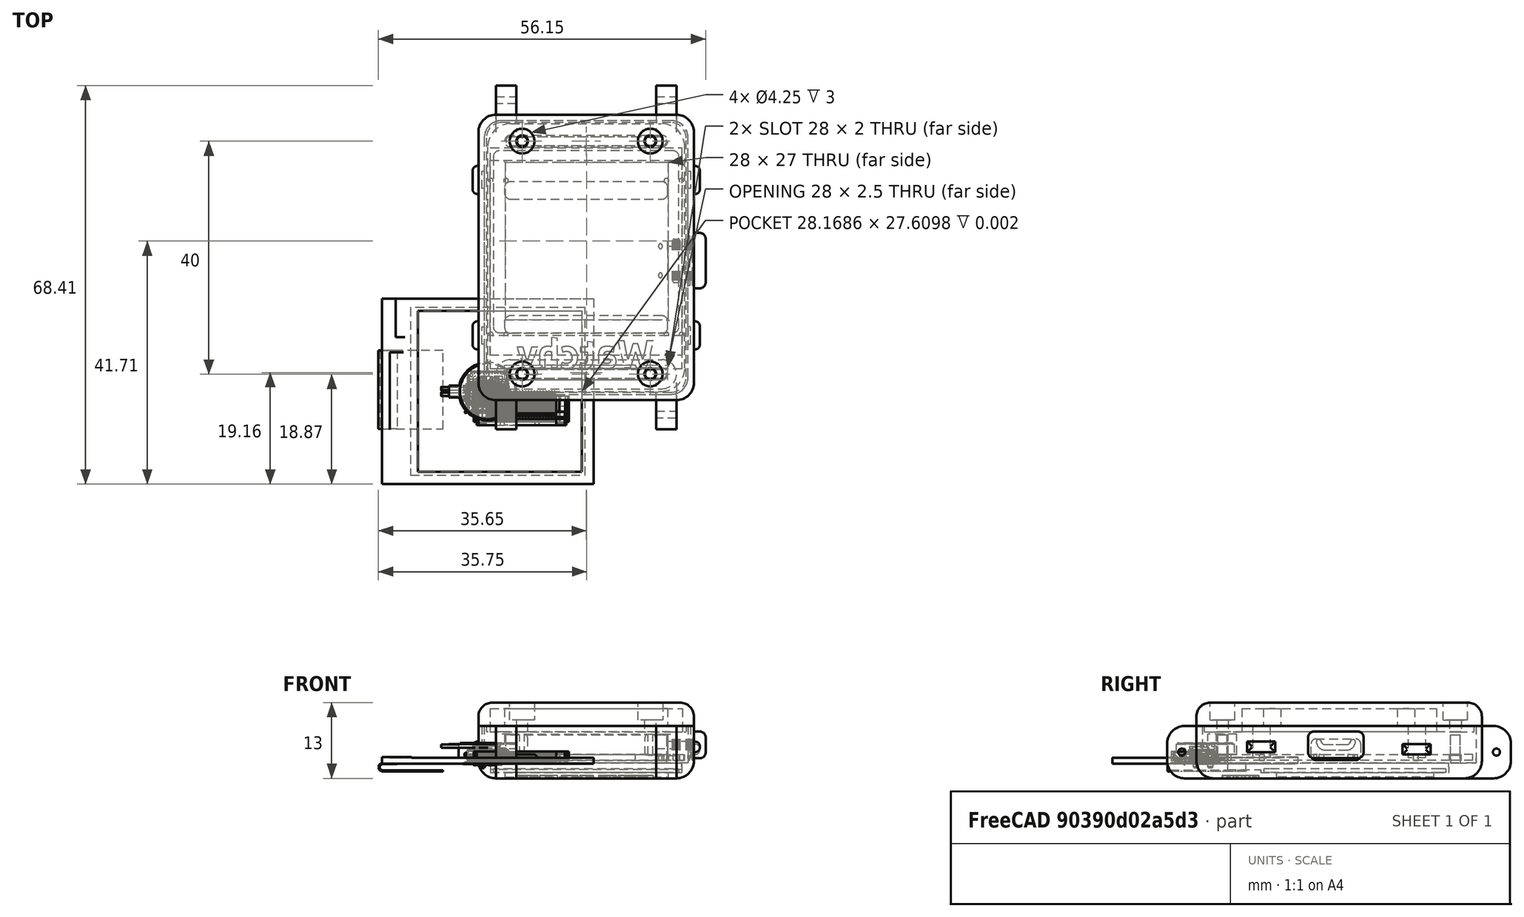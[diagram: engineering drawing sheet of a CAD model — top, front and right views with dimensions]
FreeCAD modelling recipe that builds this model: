
FCSTD DOCUMENT  (FreeCAD 0.20R29177 +426 (Git))
Label: JJ-WATCHY
License: All rights reserved
LicenseURL: http://en.wikipedia.org/wiki/All_rights_reserved
objects: Part::Feature×58, App::Part×56, Sketcher::SketchObject×26, PartDesign::Pad×21, PartDesign::Pocket×14, PartDesign::Fillet×10, PartDesign::ShapeBinder×7, PartDesign::Body×6, PartDesign::Plane×3, Part::Part2DObjectPython×1, Part::Extrusion×1, PartDesign::FeatureBase×1, Mesh::Feature×1, Part::Fuse×1, Part::Cut×1
note: 195 computed .brp shape members not serialized (recipe doc carries the construction recipe); baked Part::Feature solids carry a one-line shape summary decoded from their .brp

FEATURE [Part::Feature] Part__Feature  label="SOLID (15)"
  shape: bbox 7.981 x 5.422 x 2.941 mm, 498 faces (baked)
FEATURE [App::Part] USB_Micro_B_Molex_47346_0001  label="USB_Micro-B_Molex_47346-0001"
  Group = -> [Part__Feature]
  Origin = -> Origin
  Placement = pos=(31.38,22.43,1.65) rot=(0,0,1;1.5708rad)
FEATURE [Part::Feature] Part__Feature001  label="SOLID"
  shape: bbox 1.6 x 0.8 x 0.8 mm, 28 faces (baked)
FEATURE [App::Part] C_0603_1608Metric
  Group = -> [Part__Feature001]
  Origin = -> Origin001
  Placement = pos=(5.16,37.71,1.65) rot=(0,0,1;0rad)
FEATURE [Part::Feature] Part__Feature002  label="SOLID (16)"
  shape: bbox 6.669 x 4.906 x 2.452 mm, 452 faces (baked)
FEATURE [App::Part] Button
  Group = -> [Part__Feature002]
  Origin = -> Origin002
  Placement = pos=(2.38,35.43,1.65) rot=(0,0,-1;1.5708rad)
FEATURE [Part::Feature] Part__Feature003  label="SOLID (16)001"
  shape: bbox 6.669 x 4.906 x 2.452 mm, 452 faces (baked)
FEATURE [App::Part] Button001
  Group = -> [Part__Feature003]
  Origin = -> Origin003
  Placement = pos=(2.38,8.73,1.65) rot=(0,0,-1;1.5708rad)
FEATURE [Part::Feature] Part__Feature004  label="SOLID (16)002"
  shape: bbox 6.669 x 4.906 x 2.452 mm, 452 faces (baked)
FEATURE [App::Part] Button002
  Group = -> [Part__Feature004]
  Origin = -> Origin004
  Placement = pos=(31.42,37.23,1.65) rot=(0,0,1;1.5708rad)
FEATURE [Part::Feature] Part__Feature005  label="SOLID (16)003"
  shape: bbox 6.669 x 4.906 x 2.452 mm, 452 faces (baked)
FEATURE [App::Part] Button003
  Group = -> [Part__Feature005]
  Origin = -> Origin005
  Placement = pos=(31.42,10.53,1.65) rot=(0,0,1;1.5708rad)
FEATURE [Part::Feature] Part__Feature006  label="SOLID (1)"
  shape: bbox 2 x 2 x 1.025 mm, 68 faces (baked)
FEATURE [App::Part] LGA_12_2x2mm_P0_5mm  label="LGA-12_2x2mm_P0.5mm"
  Group = -> [Part__Feature006]
  Origin = -> Origin006
  Placement = pos=(10.76,34.89,1.65) rot=(0,0,1;3.14159rad)
FEATURE [Part::Feature] Part__Feature007  label="COMPOUND (3)"
  shape: bbox 16.3 x 5.85 x 2.11 mm, 1280 faces, 17 solids (baked)
FEATURE [App::Part] FPC_24  label="FPC-24"
  Group = -> [Part__Feature007]
  Origin = -> Origin007
  Placement = pos=(11.025,19.09,1.65) rot=(0,0,1;0rad)
FEATURE [Part::Feature] Part__Feature008  label="SOLID (4)"
  shape: bbox 7.65 x 5.2 x 3.4 mm, 136 faces (baked)
FEATURE [App::Part] Molex_PicoBlade_53261_0271_1x02_1MP_P1_25mm_Horizontal  label="Molex_PicoBlade_53261-0271_1x02-1MP_P1.25mm_Horizontal"
  Group = -> [Part__Feature008]
  Origin = -> Origin008
  Placement = pos=(28.63,31.39,1.65) rot=(0,0,-1;1.5708rad)
FEATURE [Part::Feature] Part__Feature009  label="SOLID (2)"
  shape: bbox 1 x 0.5 x 0.35 mm, 26 faces (baked)
FEATURE [App::Part] R_0402_1005Metric
  Group = -> [Part__Feature009]
  Origin = -> Origin009
  Placement = pos=(31.7,28.28,1.65) rot=(0,0,1;1.5708rad)
FEATURE [Part::Feature] Part__Feature010  label="SOLID (5)"
  shape: bbox 4 x 4 x 1.1 mm, 158 faces (baked)
FEATURE [App::Part] QFN_24_1EP_4x4mm_P0_5mm_EP2_7x2_7mm  label="QFN-24-1EP_4x4mm_P0.5mm_EP2.7x2.7mm"
  Group = -> [Part__Feature010]
  Origin = -> Origin010
  Placement = pos=(25.76,24.38,1.65) rot=(0,0,1;0rad)
FEATURE [Part::Feature] Part__Feature011  label="SOLID (2)001"
  shape: bbox 1 x 0.5 x 0.35 mm, 26 faces (baked)
FEATURE [App::Part] R_0402_1005Metric001
  Group = -> [Part__Feature011]
  Origin = -> Origin011
  Placement = pos=(29.05,13.07,1.65) rot=(0,0,1;0rad)
FEATURE [Part::Feature] Part__Feature012  label="SOLID001"
  shape: bbox 1.6 x 0.8 x 0.8 mm, 28 faces (baked)
FEATURE [App::Part] C_0603_1608Metric001
  Group = -> [Part__Feature012]
  Origin = -> Origin012
  Placement = pos=(21.71,23.42,1.65) rot=(0,0,1;0rad)
FEATURE [Part::Feature] Part__Feature013  label="COMPOUND"
  shape: bbox 37.16 x 32.08 x 2.7 mm, 57 faces, 2 solids (baked)
FEATURE [App::Part] Display
  Group = -> [Part__Feature013]
  Origin = -> Origin013
  Placement = pos=(16.89,23.15,0.55) rot=(0.707107,0.707107,0;3.14159rad)
FEATURE [Part::Feature] Part__Feature014  label="SOLID002"
  shape: bbox 1.6 x 0.8 x 0.8 mm, 28 faces (baked)
FEATURE [App::Part] C_0603_1608Metric002
  Group = -> [Part__Feature014]
  Origin = -> Origin014
  Placement = pos=(15.42,35.06,1.65) rot=(0,0,1;1.5708rad)
FEATURE [Part::Feature] Part__Feature015  label="SOLID003"
  shape: bbox 1.6 x 0.8 x 0.8 mm, 28 faces (baked)
FEATURE [App::Part] C_0603_1608Metric003
  Group = -> [Part__Feature015]
  Origin = -> Origin015
  Placement = pos=(19.01,21.47,1.65) rot=(0,0,1;1.5708rad)
FEATURE [Part::Feature] Part__Feature016  label="SOLID (3)"
  shape: bbox 2 x 1.25 x 1.25 mm, 28 faces (baked)
FEATURE [App::Part] C_0805_2012Metric
  Group = -> [Part__Feature016]
  Origin = -> Origin016
  Placement = pos=(5.63,12.59,1.65) rot=(0,0,1;0rad)
FEATURE [Part::Feature] Part__Feature017  label="SOLID (3)001"
  shape: bbox 2 x 1.25 x 1.25 mm, 28 faces (baked)
FEATURE [App::Part] C_0805_2012Metric001
  Group = -> [Part__Feature017]
  Origin = -> Origin017
  Placement = pos=(6.63,6.34,1.65) rot=(0,0,1;0rad)
FEATURE [Part::Feature] Part__Feature018  label="SOLID004"
  shape: bbox 1.6 x 0.8 x 0.8 mm, 28 faces (baked)
FEATURE [App::Part] C_0603_1608Metric004
  Group = -> [Part__Feature018]
  Origin = -> Origin018
  Placement = pos=(13.81,21.47,1.65) rot=(0,0,1;1.5708rad)
FEATURE [Part::Feature] Part__Feature019  label="SOLID005"
  shape: bbox 1.6 x 0.8 x 0.8 mm, 28 faces (baked)
FEATURE [App::Part] C_0603_1608Metric005
  Group = -> [Part__Feature019]
  Origin = -> Origin019
  Placement = pos=(16.41,21.47,1.65) rot=(0,0,1;1.5708rad)
FEATURE [Part::Feature] Part__Feature020  label="SOLID006"
  shape: bbox 1.6 x 0.8 x 0.8 mm, 28 faces (baked)
FEATURE [App::Part] C_0603_1608Metric006
  Group = -> [Part__Feature020]
  Origin = -> Origin020
  Placement = pos=(17.71,21.47,1.65) rot=(0,0,1;1.5708rad)
FEATURE [Part::Feature] Part__Feature021  label="SOLID007"
  shape: bbox 1.6 x 0.8 x 0.8 mm, 28 faces (baked)
FEATURE [App::Part] C_0603_1608Metric007
  Group = -> [Part__Feature021]
  Origin = -> Origin021
  Placement = pos=(15.11,21.47,1.65) rot=(0,0,1;1.5708rad)
FEATURE [Part::Feature] Part__Feature022  label="SOLID008"
  shape: bbox 1.6 x 0.8 x 0.8 mm, 28 faces (baked)
FEATURE [App::Part] C_0603_1608Metric008
  Group = -> [Part__Feature022]
  Origin = -> Origin022
  Placement = pos=(12.46,21.47,1.65) rot=(0,0,1;1.5708rad)
FEATURE [Part::Feature] Part__Feature023  label="SOLID009"
  shape: bbox 1.6 x 0.8 x 0.8 mm, 28 faces (baked)
FEATURE [App::Part] C_0603_1608Metric009
  Group = -> [Part__Feature023]
  Origin = -> Origin023
  Placement = pos=(11.16,21.47,1.65) rot=(0,0,1;1.5708rad)
FEATURE [Part::Feature] Part__Feature024  label="SOLID (3)002"
  shape: bbox 2 x 1.25 x 1.25 mm, 28 faces (baked)
FEATURE [App::Part] C_0805_2012Metric002
  Group = -> [Part__Feature024]
  Origin = -> Origin024
  Placement = pos=(17.82,35.53,1.65) rot=(0,0,1;3.14159rad)
FEATURE [Part::Feature] Part__Feature025  label="SOLID (6)"
  shape: bbox 3.8 x 1.6 x 1.25 mm, 67 faces (baked)
FEATURE [App::Part] D_SOD_123  label="D_SOD-123"
  Group = -> [Part__Feature025]
  Origin = -> Origin025
  Placement = pos=(1.25,15.82,1.65) rot=(0,0,1;1.5708rad)
FEATURE [Part::Feature] Part__Feature026  label="SOLID (6)001"
  shape: bbox 3.8 x 1.6 x 1.25 mm, 67 faces (baked)
FEATURE [App::Part] D_SOD_123001  label="D_SOD-124"
  Group = -> [Part__Feature026]
  Origin = -> Origin026
  Placement = pos=(3.55,15.82,1.65) rot=(0,0,-1;1.5708rad)
FEATURE [Part::Feature] Part__Feature027  label="SOLID (6)002"
  shape: bbox 3.8 x 1.6 x 1.25 mm, 67 faces (baked)
FEATURE [App::Part] D_SOD_123002  label="D_SOD-125"
  Group = -> [Part__Feature027]
  Origin = -> Origin027
  Placement = pos=(5.85,15.82,1.65) rot=(0,0,-1;1.5708rad)
FEATURE [Part::Feature] Part__Feature028  label="SOLID (6)003"
  shape: bbox 3.8 x 1.6 x 1.25 mm, 67 faces (baked)
FEATURE [App::Part] D_SOD_123003  label="D_SOD-126"
  Group = -> [Part__Feature028]
  Origin = -> Origin028
  Placement = pos=(27.27,19.28,1.65) rot=(0,0,1;1.5708rad)
FEATURE [Part::Feature] Part__Feature029  label="SOLID (7)"
  shape: bbox 1.6 x 0.8 x 1.1 mm, 50 faces (baked)
FEATURE [App::Part] LED_0603_1608Metric
  Group = -> [Part__Feature029]
  Origin = -> Origin029
  Placement = pos=(33.04,30.53,1.65) rot=(0,0,1;1.5708rad)
FEATURE [Part::Feature] Part__Feature030  label="SOLID (8)"
  shape: bbox 3.5 x 1.6 x 1.1 mm, 27 faces (baked)
FEATURE [App::Part] D_SOD_123F  label="D_SOD-123F"
  Group = -> [Part__Feature030]
  Origin = -> Origin030
  Placement = pos=(4.91,34.705,1.65) rot=(0,0,-1;1.5708rad)
FEATURE [Part::Feature] Part__Feature031  label="SOLID (9)"
  shape: bbox 3.2 x 2.5 x 2.5 mm, 28 faces (baked)
FEATURE [App::Part] L_1210_3225Metric
  Group = -> [Part__Feature031]
  Origin = -> Origin031
  Placement = pos=(6.13,9.47,1.65) rot=(0,0,-1;1.5708rad)
FEATURE [Part::Feature] Part__Feature032  label="SOLID (10)"
  shape: bbox 2.5 x 3 x 1.2 mm, 76 faces (baked)
FEATURE [App::Part] SOT_23  label="SOT-23"
  Group = -> [Part__Feature032]
  Origin = -> Origin032
  Placement = pos=(28.1,9.03,1.65) rot=(0,0,-1;1.5708rad)
FEATURE [Part::Feature] Part__Feature033  label="SOLID (10)001"
  shape: bbox 2.5 x 3 x 1.2 mm, 76 faces (baked)
FEATURE [App::Part] SOT_23001  label="SOT-024"
  Group = -> [Part__Feature033]
  Origin = -> Origin033
  Placement = pos=(28.45,15.23,1.65) rot=(0,0,-1;1.5708rad)
FEATURE [Part::Feature] Part__Feature034  label="SOLID (10)002"
  shape: bbox 2.5 x 3 x 1.2 mm, 76 faces (baked)
FEATURE [App::Part] SOT_23002  label="SOT-025"
  Group = -> [Part__Feature034]
  Origin = -> Origin034
  Placement = pos=(7.81,35.31,1.65) rot=(0,0,1;3.14159rad)
FEATURE [Part::Feature] Part__Feature035  label="SOLID (2)002"
  shape: bbox 1 x 0.5 x 0.35 mm, 26 faces (baked)
FEATURE [App::Part] R_0402_1005Metric002
  Group = -> [Part__Feature035]
  Origin = -> Origin035
  Placement = pos=(16.97,34.19,1.65) rot=(0,0,1;3.14159rad)
FEATURE [Part::Feature] Part__Feature036  label="SOLID (2)003"
  shape: bbox 1 x 0.5 x 0.35 mm, 26 faces (baked)
FEATURE [App::Part] R_0402_1005Metric003
  Group = -> [Part__Feature036]
  Origin = -> Origin036
  Placement = pos=(22.55,26.67,1.65) rot=(0,0,1;1.5708rad)
FEATURE [Part::Feature] Part__Feature037  label="SOLID (2)004"
  shape: bbox 1 x 0.5 x 0.35 mm, 26 faces (baked)
FEATURE [App::Part] R_0402_1005Metric004
  Group = -> [Part__Feature037]
  Origin = -> Origin037
  Placement = pos=(23.91,27.48,1.65) rot=(0,0,1;3.14159rad)
FEATURE [Part::Feature] Part__Feature038  label="SOLID (2)005"
  shape: bbox 1 x 0.5 x 0.35 mm, 26 faces (baked)
FEATURE [App::Part] R_0402_1005Metric005
  Group = -> [Part__Feature038]
  Origin = -> Origin038
  Placement = pos=(27.15,13.07,1.65) rot=(0,0,1;3.14159rad)
FEATURE [Part::Feature] Part__Feature039  label="SOLID (2)006"
  shape: bbox 1 x 0.5 x 0.35 mm, 26 faces (baked)
FEATURE [App::Part] R_0402_1005Metric006
  Group = -> [Part__Feature039]
  Origin = -> Origin039
  Placement = pos=(28.66,36.44,1.65) rot=(0,0,1;0rad)
FEATURE [Part::Feature] Part__Feature040  label="SOLID (2)007"
  shape: bbox 1 x 0.5 x 0.35 mm, 26 faces (baked)
FEATURE [App::Part] R_0402_1005Metric007
  Group = -> [Part__Feature040]
  Origin = -> Origin040
  Placement = pos=(6.69,32.68,1.65) rot=(0,0,-1;1.5708rad)
FEATURE [Part::Feature] Part__Feature041  label="SOLID (2)008"
  shape: bbox 1 x 0.5 x 0.35 mm, 26 faces (baked)
FEATURE [App::Part] R_0402_1005Metric008
  Group = -> [Part__Feature041]
  Origin = -> Origin041
  Placement = pos=(29.05,11.28,1.65) rot=(0,0,1;3.14159rad)
FEATURE [Part::Feature] Part__Feature042  label="SOLID (2)009"
  shape: bbox 1 x 0.5 x 0.35 mm, 26 faces (baked)
FEATURE [App::Part] R_0402_1005Metric009
  Group = -> [Part__Feature042]
  Origin = -> Origin042
  Placement = pos=(27.15,11.28,1.65) rot=(0,0,1;3.14159rad)
FEATURE [Part::Feature] Part__Feature043  label="SOLID (2)010"
  shape: bbox 1 x 0.5 x 0.35 mm, 26 faces (baked)
FEATURE [App::Part] R_0402_1005Metric010
  Group = -> [Part__Feature043]
  Origin = -> Origin043
  Placement = pos=(4.35,6.34,1.65) rot=(0,0,1;1.5708rad)
FEATURE [Part::Feature] Part__Feature044  label="SOLID (2)011"
  shape: bbox 1 x 0.5 x 0.35 mm, 26 faces (baked)
FEATURE [App::Part] R_0402_1005Metric011
  Group = -> [Part__Feature044]
  Origin = -> Origin044
  Placement = pos=(30.8,28.28,1.65) rot=(0,0,1;1.5708rad)
FEATURE [Part::Feature] Part__Feature045  label="SOLID (2)012"
  shape: bbox 1 x 0.5 x 0.35 mm, 26 faces (baked)
FEATURE [App::Part] R_0402_1005Metric012
  Group = -> [Part__Feature045]
  Origin = -> Origin045
  Placement = pos=(29.32,17.4,1.65) rot=(0,0,1;3.14159rad)
FEATURE [Part::Feature] Part__Feature046  label="SOLID (2)013"
  shape: bbox 1 x 0.5 x 0.35 mm, 26 faces (baked)
FEATURE [App::Part] R_0402_1005Metric013
  Group = -> [Part__Feature046]
  Origin = -> Origin046
  Placement = pos=(33.24,28.28,1.65) rot=(0,0,-1;1.5708rad)
FEATURE [Part::Feature] Part__Feature047  label="SOLID (2)014"
  shape: bbox 1 x 0.5 x 0.35 mm, 26 faces (baked)
FEATURE [App::Part] R_0402_1005Metric014
  Group = -> [Part__Feature047]
  Origin = -> Origin047
  Placement = pos=(7.75,32.68,1.65) rot=(0,0,-1;1.5708rad)
FEATURE [Part::Feature] Part__Feature048  label="SOLID (13)"
  shape: bbox 7 x 7 x 0.77 mm, 302 faces (baked)
FEATURE [App::Part] QFN_48_1EP_7x7mm_P0_5mm_EP5_15x5_15mm  label="QFN-48-1EP_7x7mm_P0.5mm_EP5.15x5.15mm"
  Group = -> [Part__Feature048]
  Origin = -> Origin048
  Placement = pos=(17.7737,29.6588,1.65) rot=(0,0,-1;1.5708rad)
FEATURE [Part::Feature] Part__Feature049  label="SOLID (11)"
  shape: bbox 2.8 x 2.9 x 1.55 mm, 109 faces (baked)
FEATURE [App::Part] SOT_23_5  label="SOT-23-5"
  Group = -> [Part__Feature049]
  Origin = -> Origin049
  Placement = pos=(24.66,19.88,1.65) rot=(0,0,-1;1.5708rad)
FEATURE [Part::Feature] Part__Feature050  label="SOLID (11)001"
  shape: bbox 2.8 x 2.9 x 1.55 mm, 109 faces (baked)
FEATURE [App::Part] SOT_23_5001  label="SOT-23-006"
  Group = -> [Part__Feature050]
  Origin = -> Origin050
  Placement = pos=(32,15.93,1.65) rot=(0,0,-1;1.5708rad)
FEATURE [Part::Feature] Part__Feature051  label="SOLID (12)"
  shape: bbox 2 x 2 x 1.05 mm, 118 faces (baked)
FEATURE [App::Part] SOT_363_SC_70_6  label="SOT-363_SC-70-6"
  Group = -> [Part__Feature051]
  Origin = -> Origin051
  Placement = pos=(21.31,21.47,1.65) rot=(0,0,1;3.14159rad)
FEATURE [Part::Feature] Part__Feature052  label="SOLID (14)"
  shape: bbox 6 x 4.9 x 1.75 mm, 156 faces (baked)
FEATURE [App::Part] SOIC_8_3_9x4_9mm_P1_27mm  label="SOIC-8_3.9x4.9mm_P1.27mm"
  Group = -> [Part__Feature052]
  Origin = -> Origin052
  Placement = pos=(11.07,29.81,1.65) rot=(0,0,1;1.5708rad)
FEATURE [Part::Feature] Part__Feature053  label="SOLID (2)015"
  shape: bbox 1 x 0.5 x 0.35 mm, 26 faces (baked)
FEATURE [App::Part] R_0402_1005Metric015
  Group = -> [Part__Feature053]
  Origin = -> Origin053
  Placement = pos=(7.75,30.52,1.65) rot=(0,0,-1;1.5708rad)
FEATURE [Part::Feature] Part__Feature054  label="COMPOUND (1)"
  shape: bbox 13 x 10 x 2.5 mm, 15 faces, 3 solids (baked)
FEATURE [App::Part] PagerMotor
  Group = -> [Part__Feature054]
  Origin = -> Origin054
  Placement = pos=(5.45,22.955,5.15) rot=(0.819152,-0.573576,0;3.14159rad)
FEATURE [Part::Feature] Part__Feature055  label="COMPOUND (2)"
  shape: bbox 33.8 x 45.96 x 1 mm, 46 faces (baked)
FEATURE [App::Part] Watchy_Fixed_Dimensions_v1  label="Watchy Fixed Dimensions v1"
  Group = -> [USB_Micro_B_Molex_47346_0001,C_0603_1608Metric,Button,Button001,Button002,Button003,LGA_12_2x2mm_P0_5mm,FPC_24,Molex_PicoBlade_53261_0271_1x02_1MP_P1_25mm_Horizontal,R_0402_1005Metric,QFN_24_1EP_4x4mm_P0_5mm_EP2_7x2_7mm,R_0402_1005Metric001,C_0603_1608Metric001,Display,C_0603_1608Metric002,C_0603_1608Metric003,C_0805_2012Metric,C_0805_2012Metric001,C_0603_1608Metric004,C_0603_1608Metric005,+36 more]
  Origin = -> Origin055
  Placement = pos=(0,0,-0.43) rot=(0,0,1;0rad)
FEATURE [Sketcher::SketchObject] Sketch
  FullyConstrained = true
  MapMode = 5
  Placement = pos=(0,0,0) rot=(0,1,0;3.14159rad)
  Support = -> [XY_Plane056]
  sketch-geometry (4):
    g0: LineSegment StartX=-32.81 StartY=41.31 StartZ=0 EndX=-0.98 EndY=41.31 EndZ=0
    g1: LineSegment StartX=-0.98 StartY=41.31 StartZ=0 EndX=-0.98 EndY=10.07 EndZ=0
    g2: LineSegment StartX=-0.98 StartY=10.07 StartZ=0 EndX=-32.81 EndY=10.07 EndZ=0
    g3: LineSegment StartX=-32.81 StartY=10.07 StartZ=0 EndX=-32.81 EndY=41.31 EndZ=0
  constraints (12):
    c: Coincident(g0,g1)
    c: Coincident(g1,g2)
    c: Coincident(g2,g3)
    c: Coincident(g3,g0)
    c: Horizontal(g0)
    c: Horizontal(g2)
    c: Vertical(g1)
    c: Vertical(g3)
    c: DistanceX(g0,g0) = 31.83
    c: DistanceY(g1,g1) = 31.24
    c: DistanceY(g-1,g1) = 10.07
    c: DistanceX(g1,g-1) = 0.98
FEATURE [PartDesign::Pad] Pad
  Direction = (0,0,-1)
  Length = 1.5
  Length2 = 10
  Profile = -> Sketch
  ReferenceAxis = -> Sketch [N_Axis]
  Type = 0
FEATURE [PartDesign::Fillet] Fillet
  Base = -> Pad [Edge1,Edge2,Edge5,Edge8]
  BaseFeature = -> Pad
  Radius = 1
  SupportTransform = false
  UseAllEdges = false
FEATURE [PartDesign::Pocket] Pocket
  BaseFeature = -> Fillet
  Direction = (0,0,-1)
  Length = 0.9
  Length2 = 5
  Profile = -> Fillet [Face2]
  Type = 0
FEATURE [PartDesign::ShapeBinder] ReferencePocket
  Placement = pos=(0,0,-1.5) rot=(0,0,1;0rad)
  Support = -> [Pocket]
  TraceSupport = false
FEATURE [PartDesign::Plane] DatumPlane
  Length = 73.6348
  MapMode = 5
  Placement = pos=(0,0,-1.5) rot=(1,0,0;3.14159rad)
  ResizeMode = 0
  Support = -> [ReferencePocket]
  Width = 85.7348
FEATURE [Sketcher::SketchObject] Sketch001
  ExternalGeometry = -> [ReferencePocket]
  FullyConstrained = true
  MapMode = 5
  Placement = pos=(0,0,-1.5) rot=(1,0,0;3.14159rad)
  Support = -> [DatumPlane]
  sketch-geometry (5):
    g0: LineSegment StartX=-1.6 StartY=1.5 StartZ=0 EndX=35.4 EndY=1.5 EndZ=0
    g1: LineSegment StartX=35.4 StartY=1.5 StartZ=0 EndX=35.4 EndY=-47.5 EndZ=0
    g2: LineSegment StartX=35.4 StartY=-47.5 StartZ=0 EndX=-1.6 EndY=-47.5 EndZ=0
    g3: LineSegment StartX=-1.6 StartY=-47.5 StartZ=0 EndX=-1.6 EndY=1.5 EndZ=0
    g4: GeomPoint X=16.9 Y=-23 Z=0
  constraints (13):
    c: Coincident(g0,g1)
    c: Coincident(g1,g2)
    c: Coincident(g2,g3)
    c: Coincident(g3,g0)
    c: Horizontal(g0)
    c: Horizontal(g2)
    c: Vertical(g1)
    c: Vertical(g3)
    c: DistanceX(g0,g0) = 37
    c: DistanceY(g1,g1) = 49
    c: DistanceX(g-1,g4) = 16.9
    c: DistanceY(g4,g-1) = 23
    c: Symmetric(g2,g0,g4)
FEATURE [PartDesign::Pad] Pad001
  Direction = (0,0,-1)
  Length = 1
  Length2 = 8
  Placement = pos=(0,0,-1.5) rot=(1,0,0;3.14159rad)
  Profile = -> Sketch001
  ReferenceAxis = -> Sketch001 [N_Axis]
  Type = 4
FEATURE [Sketcher::SketchObject] Sketch002
  FullyConstrained = true
  MapMode = 5
  Placement = pos=(0,0,-2.5) rot=(1,0,0;3.14159rad)
  Support = -> [Pad001]
  sketch-geometry (5):
    g0: LineSegment StartX=3 StartY=-12.3 StartZ=0 EndX=31 EndY=-12.3 EndZ=0
    g1: LineSegment StartX=31 StartY=-12.3 StartZ=0 EndX=31 EndY=-39.3 EndZ=0
    g2: LineSegment StartX=31 StartY=-39.3 StartZ=0 EndX=3 EndY=-39.3 EndZ=0
    g3: LineSegment StartX=3 StartY=-39.3 StartZ=0 EndX=3 EndY=-12.3 EndZ=0
    g4: GeomPoint X=17 Y=-25.8 Z=0
  constraints (13):
    c: Coincident(g0,g1)
    c: Coincident(g1,g2)
    c: Coincident(g2,g3)
    c: Coincident(g3,g0)
    c: Horizontal(g0)
    c: Horizontal(g2)
    c: Vertical(g1)
    c: Vertical(g3)
    c: DistanceX(g0,g0) = 28
    c: DistanceY(g1,g1) = 27
    c: DistanceX(g-1,g4) = 17
    c: DistanceY(g4,g-1) = 25.8
    c: Symmetric(g2,g0,g4)
FEATURE [PartDesign::Pocket] Pocket001
  BaseFeature = -> Pad001
  Direction = (0,-1e-16,1)
  Length = 1
  Length2 = 5
  Placement = pos=(0,0,-1.5) rot=(1,0,0;3.14159rad)
  Profile = -> Sketch002
  ReferenceAxis = -> Sketch002 [N_Axis]
  Type = 0
FEATURE [Sketcher::SketchObject] Sketch003
  ExternalGeometry = -> [Pocket001]
  FullyConstrained = true
  MapMode = 5
  Placement = pos=(0,0,6.5) rot=(0,0,1;0rad)
  Support = -> [Pocket001]
  sketch-geometry (5):
    g0: LineSegment StartX=-0.6 StartY=46.5 StartZ=0 EndX=-0.6 EndY=-0.5 EndZ=0
    g1: LineSegment StartX=-0.6 StartY=-0.5 StartZ=0 EndX=34.4 EndY=-0.5 EndZ=0
    g2: LineSegment StartX=34.4 StartY=-0.5 StartZ=0 EndX=34.4 EndY=46.5 EndZ=0
    g3: LineSegment StartX=34.4 StartY=46.5 StartZ=0 EndX=-0.6 EndY=46.5 EndZ=0
    g4: Circle CenterX=16.9 CenterY=23 CenterZ=0 NormalX=0 NormalY=0 NormalZ=1 AngleXU=0 Radius=29.3002
  constraints (14):
    c: Coincident(g0,g1)
    c: Coincident(g1,g2)
    c: Coincident(g2,g3)
    c: Coincident(g3,g0)
    c: PointOnObject(g0,g4)
    c: PointOnObject(g1,g4)
    c: PointOnObject(g2,g4)
    c: PointOnObject(g3,g4)
    c: Horizontal(g3)
    c: Horizontal(g1)
    c: Vertical(g2)
    c: DistanceX(g3,g3) = 35
    c: DistanceY(g2,g2) = 47
    c: Symmetric(g-3,g-4,g4)
FEATURE [PartDesign::Pocket] Pocket002
  BaseFeature = -> Pocket001
  Direction = (0,2e-16,-1)
  Length = 7
  Length2 = 5
  Placement = pos=(0,0,-1.5) rot=(1,0,0;3.14159rad)
  Profile = -> Sketch003
  ReferenceAxis = -> Sketch003 [N_Axis]
  Type = 0
FEATURE [Sketcher::SketchObject] Sketch004
  ExternalGeometry = -> [ReferencePocket]
  FullyConstrained = true
  MapMode = 5
  Placement = pos=(0,-2e-16,-0.5) rot=(0,0,1;0rad)
  Support = -> [Pocket002]
  sketch-geometry (4):
    g0: LineSegment StartX=0.48 StartY=41.81 StartZ=0 EndX=33.31 EndY=41.81 EndZ=0
    g1: LineSegment StartX=33.31 StartY=41.81 StartZ=0 EndX=33.31 EndY=9.57 EndZ=0
    g2: LineSegment StartX=33.31 StartY=9.57 StartZ=0 EndX=0.48 EndY=9.57 EndZ=0
    g3: LineSegment StartX=0.48 StartY=9.57 StartZ=0 EndX=0.48 EndY=41.81 EndZ=0
  constraints (12):
    c: Coincident(g0,g1)
    c: Coincident(g1,g2)
    c: Coincident(g2,g3)
    c: Coincident(g3,g0)
    c: Horizontal(g0)
    c: Horizontal(g2)
    c: Vertical(g1)
    c: Vertical(g3)
    c: DistanceX(g0,g-4) = 0.5
    c: DistanceX(g-6,g0) = 0.5
    c: DistanceY(g-3,g0) = 0.5
    c: DistanceY(g1,g-5) = 0.5
FEATURE [PartDesign::Pocket] Pocket003
  BaseFeature = -> Pocket002
  Direction = (0,4e-16,-1)
  Length = 1
  Length2 = 5
  Placement = pos=(0,0,-1.5) rot=(1,0,0;3.14159rad)
  Profile = -> Sketch004
  ReferenceAxis = -> Sketch004 [N_Axis]
  Type = 0
FEATURE [Sketcher::SketchObject] Sketch005
  FullyConstrained = true
  MapMode = 5
  Placement = pos=(34.4,0,-1.5) rot=(0.57735,0.57735,-0.57735;4.18879rad)
  Support = -> [Pocket003]
  sketch-geometry (4):
    g0: LineSegment StartX=18.2 StartY=-2.15 StartZ=0 EndX=26.7 EndY=-2.15 EndZ=0
    g1: LineSegment StartX=26.7 StartY=-2.15 StartZ=0 EndX=26.7 EndY=-5.75 EndZ=0
    g2: LineSegment StartX=26.7 StartY=-5.75 StartZ=0 EndX=18.2 EndY=-5.75 EndZ=0
    g3: LineSegment StartX=18.2 StartY=-5.75 StartZ=0 EndX=18.2 EndY=-2.15 EndZ=0
  constraints (12):
    c: Coincident(g0,g1)
    c: Coincident(g1,g2)
    c: Coincident(g2,g3)
    c: Coincident(g3,g0)
    c: Horizontal(g0)
    c: Horizontal(g2)
    c: Vertical(g1)
    c: Vertical(g3)
    c: DistanceX(g2,g2) = 8.5
    c: DistanceY(g1,g1) = 3.6
    c: DistanceX(g-1,g0) = 18.2
    c: DistanceY(g0,g-1) = 2.15
FEATURE [PartDesign::Pocket] Pocket004
  BaseFeature = -> Pocket003
  Direction = (1,0,0)
  Length = 5
  Length2 = 5
  Placement = pos=(0,0,-1.5) rot=(1,0,0;3.14159rad)
  Profile = -> Sketch005
  ReferenceAxis = -> Sketch005 [N_Axis]
  Type = 0
FEATURE [Sketcher::SketchObject] Sketch006
  ExternalGeometry = -> [Pocket004]
  FullyConstrained = true
  MapMode = 5
  Placement = pos=(0,0,6.5) rot=(0,0,1;0rad)
  Support = -> [Pocket004]
  sketch-geometry (20):
    g0: LineSegment StartX=-1 StartY=37.83 StartZ=0 EndX=-0.6 EndY=37.83 EndZ=0
    g1: LineSegment StartX=-0.6 StartY=37.83 StartZ=0 EndX=-0.6 EndY=34.83 EndZ=0
    g2: LineSegment StartX=-0.6 StartY=34.83 StartZ=0 EndX=-1 EndY=34.83 EndZ=0
    g3: LineSegment StartX=-1 StartY=34.83 StartZ=0 EndX=-1 EndY=37.83 EndZ=0
    g4: LineSegment StartX=34.4 StartY=37.83 StartZ=0 EndX=34.8 EndY=37.83 EndZ=0
    g5: LineSegment StartX=34.8 StartY=37.83 StartZ=0 EndX=34.8 EndY=34.83 EndZ=0
    g6: LineSegment StartX=34.8 StartY=34.83 StartZ=0 EndX=34.4 EndY=34.83 EndZ=0
    g7: LineSegment StartX=34.4 StartY=34.83 StartZ=0 EndX=34.4 EndY=37.83 EndZ=0
    g8: LineSegment StartX=34.4 StartY=8.13 StartZ=0 EndX=34.8 EndY=8.13 EndZ=0
    g9: LineSegment StartX=34.8 StartY=8.13 StartZ=0 EndX=34.8 EndY=11.13 EndZ=0
    g10: LineSegment StartX=34.8 StartY=11.13 StartZ=0 EndX=34.4 EndY=11.13 EndZ=0
    g11: LineSegment StartX=34.4 StartY=11.13 StartZ=0 EndX=34.4 EndY=8.13 EndZ=0
    g12: LineSegment StartX=-1 StartY=11.13 StartZ=0 EndX=-0.6 EndY=11.13 EndZ=0
    g13: LineSegment StartX=-0.6 StartY=11.13 StartZ=0 EndX=-0.6 EndY=8.13 EndZ=0
    g14: LineSegment StartX=-0.6 StartY=8.13 StartZ=0 EndX=-1 EndY=8.13 EndZ=0
    g15: LineSegment StartX=-1 StartY=8.13 StartZ=0 EndX=-1 EndY=11.13 EndZ=0
    g16: Circle CenterX=-0.8 CenterY=9.63 CenterZ=0 NormalX=0 NormalY=0 NormalZ=1 AngleXU=0 Radius=1.51327
    g17: Circle CenterX=34.6 CenterY=9.63 CenterZ=0 NormalX=0 NormalY=0 NormalZ=1 AngleXU=0 Radius=1.51327
    g18: Circle CenterX=34.6 CenterY=36.33 CenterZ=0 NormalX=0 NormalY=0 NormalZ=1 AngleXU=0 Radius=1.51327
    g19: Circle CenterX=-0.8 CenterY=36.33 CenterZ=0 NormalX=0 NormalY=0 NormalZ=1 AngleXU=0 Radius=1.51327
  constraints (60):
    c: Coincident(g0,g1)
    c: Coincident(g1,g2)
    c: Coincident(g2,g3)
    c: Coincident(g3,g0)
    c: Horizontal(g0)
    c: Horizontal(g2)
    c: Vertical(g1)
    c: Vertical(g3)
    c: PointOnObject(g0,g-3)
    c: DistanceX(g0,g0) = 0.4
    c: DistanceY(g3,g3) = 3
    c: Coincident(g4,g5)
    c: Coincident(g5,g6)
    c: Coincident(g6,g7)
    c: Coincident(g7,g4)
    c: Horizontal(g4)
    c: Horizontal(g6)
    c: Vertical(g5)
    c: Vertical(g7)
    c: Coincident(g8,g9)
    c: Coincident(g9,g10)
    c: Coincident(g10,g11)
    c: Coincident(g11,g8)
    c: Horizontal(g8)
    c: Horizontal(g10)
    c: Vertical(g9)
    c: Vertical(g11)
    c: Coincident(g12,g13)
    c: Coincident(g13,g14)
    c: Coincident(g14,g15)
    c: Coincident(g15,g12)
    c: Horizontal(g12)
    c: Horizontal(g14)
    c: Vertical(g13)
    c: Vertical(g15)
    c: Equal(g0,g12)
    c: Equal(g12,g4)
    c: Equal(g4,g8)
    c: Equal(g3,g13)
    c: Equal(g13,g5)
    c: Equal(g5,g9)
    c: PointOnObject(g12,g-3)
    c: PointOnObject(g4,g-4)
    c: PointOnObject(g8,g-4)
    c: PointOnObject(g12,g16)
    c: PointOnObject(g12,g16)
    c: PointOnObject(g14,g16)
    c: DistanceY(g-1,g16) = 9.63
    c: PointOnObject(g9,g17)
    c: PointOnObject(g10,g17)
    c: PointOnObject(g8,g17)
    c: PointOnObject(g4,g18)
    c: PointOnObject(g4,g18)
    c: PointOnObject(g5,g18)
    c: PointOnObject(g0,g19)
    c: PointOnObject(g0,g19)
    c: PointOnObject(g2,g19)
    c: DistanceY(g-1,g19) = 36.33
    c: DistanceY(g-1,g18) = 36.33
    c: DistanceY(g-1,g17) = 9.63
FEATURE [PartDesign::Pocket] Pocket005
  BaseFeature = -> Pocket004
  Direction = (0,0,-1)
  Length = 5.5
  Length2 = 5
  Placement = pos=(0,0,-1.5) rot=(1,0,0;3.14159rad)
  Profile = -> Sketch006
  ReferenceAxis = -> Sketch006 [N_Axis]
  Type = 0
FEATURE [Sketcher::SketchObject] Sketch007
  FullyConstrained = true
  MapMode = 5
  Placement = pos=(-1.6,0,-1.5) rot=(0.57735,0.57735,-0.57735;4.18879rad)
  Support = -> [Pocket005]
  sketch-geometry (8):
    g0: LineSegment StartX=7.23 StartY=-3.5 StartZ=0 EndX=12.03 EndY=-3.5 EndZ=0
    g1: LineSegment StartX=12.03 StartY=-3.5 StartZ=0 EndX=12.03 EndY=-5.3 EndZ=0
    g2: LineSegment StartX=12.03 StartY=-5.3 StartZ=0 EndX=7.23 EndY=-5.3 EndZ=0
    g3: LineSegment StartX=7.23 StartY=-5.3 StartZ=0 EndX=7.23 EndY=-3.5 EndZ=0
    g4: LineSegment StartX=33.9 StartY=-3.1 StartZ=0 EndX=38.7 EndY=-3.1 EndZ=0
    g5: LineSegment StartX=38.7 StartY=-3.1 StartZ=0 EndX=38.7 EndY=-4.9 EndZ=0
    g6: LineSegment StartX=38.7 StartY=-4.9 StartZ=0 EndX=33.9 EndY=-4.9 EndZ=0
    g7: LineSegment StartX=33.9 StartY=-4.9 StartZ=0 EndX=33.9 EndY=-3.1 EndZ=0
  constraints (24):
    c: Coincident(g0,g1)
    c: Coincident(g1,g2)
    c: Coincident(g2,g3)
    c: Coincident(g3,g0)
    c: Horizontal(g0)
    c: Horizontal(g2)
    c: Vertical(g1)
    c: Vertical(g3)
    c: Coincident(g4,g5)
    c: Coincident(g5,g6)
    c: Coincident(g6,g7)
    c: Coincident(g7,g4)
    c: Horizontal(g4)
    c: Horizontal(g6)
    c: Vertical(g5)
    c: Vertical(g7)
    c: DistanceX(g2,g2) = 4.8
    c: DistanceY(g1,g1) = 1.8
    c: Equal(g1,g7)
    c: Equal(g2,g6)
    c: DistanceY(g0,g-1) = 3.5
    c: DistanceY(g4,g-1) = 3.1
    c: DistanceX(g-1,g0) = 7.23
    c: DistanceX(g-1,g4) = 33.9
FEATURE [PartDesign::Pad] Pad002
  BaseFeature = -> Pocket005
  Direction = (-1,0,0)
  Length = 1
  Length2 = 10
  Placement = pos=(0,0,-1.5) rot=(1,0,0;3.14159rad)
  Profile = -> Sketch007
  ReferenceAxis = -> Sketch007 [N_Axis]
  Type = 0
FEATURE [Sketcher::SketchObject] Sketch008
  ExternalGeometry = -> [Pad002]
  FullyConstrained = true
  MapMode = 5
  Placement = pos=(35.4,0,-1.5) rot=(0.57735,-0.57735,0.57735;4.18879rad)
  Support = -> [Pad002]
  sketch-geometry (8):
    g0: LineSegment StartX=-12.03 StartY=-3.5 StartZ=0 EndX=-7.23 EndY=-3.5 EndZ=0
    g1: LineSegment StartX=-7.23 StartY=-3.5 StartZ=0 EndX=-7.23 EndY=-5.3 EndZ=0
    g2: LineSegment StartX=-7.23 StartY=-5.3 StartZ=0 EndX=-12.03 EndY=-5.3 EndZ=0
    g3: LineSegment StartX=-12.03 StartY=-5.3 StartZ=0 EndX=-12.03 EndY=-3.5 EndZ=0
    g4: LineSegment StartX=-38.7 StartY=-3.1 StartZ=0 EndX=-33.9 EndY=-3.1 EndZ=0
    g5: LineSegment StartX=-33.9 StartY=-3.1 StartZ=0 EndX=-33.9 EndY=-4.9 EndZ=0
    g6: LineSegment StartX=-33.9 StartY=-4.9 StartZ=0 EndX=-38.7 EndY=-4.9 EndZ=0
    g7: LineSegment StartX=-38.7 StartY=-4.9 StartZ=0 EndX=-38.7 EndY=-3.1 EndZ=0
  constraints (20):
    c: Coincident(g0,g1)
    c: Coincident(g1,g2)
    c: Coincident(g2,g3)
    c: Coincident(g3,g0)
    c: Horizontal(g0)
    c: Horizontal(g2)
    c: Vertical(g1)
    c: Vertical(g3)
    c: Coincident(g0,g-4)
    c: Coincident(g1,g-6)
    c: Coincident(g4,g5)
    c: Coincident(g5,g6)
    c: Coincident(g6,g7)
    c: Coincident(g7,g4)
    c: Horizontal(g4)
    c: Horizontal(g6)
    c: Vertical(g5)
    c: Vertical(g7)
    c: Coincident(g4,g-8)
    c: Coincident(g5,g-7)
FEATURE [PartDesign::Pad] Pad003
  BaseFeature = -> Pad002
  Direction = (1,0,0)
  Length = 1
  Length2 = 10
  Placement = pos=(0,0,-1.5) rot=(1,0,0;3.14159rad)
  Profile = -> Sketch008
  ReferenceAxis = -> Sketch008 [N_Axis]
  Type = 0
FEATURE [PartDesign::Fillet] Fillet001
  Base = -> Pad003 [Edge5,Edge105,Edge18,Edge124,Edge1,Edge2,Edge116,Edge103]
  BaseFeature = -> Pad003
  Placement = pos=(0,0,-1.5) rot=(1,0,0;3.14159rad)
  Radius = 3
  SupportTransform = false
  UseAllEdges = false
FEATURE [PartDesign::Fillet] Fillet002
  Base = -> Fillet001 [Edge41]
  BaseFeature = -> Fillet001
  Placement = pos=(0,0,-1.5) rot=(1,0,0;3.14159rad)
  Radius = 3
  SupportTransform = false
  UseAllEdges = false
FEATURE [PartDesign::Fillet] Fillet003
  Base = -> Fillet002 [Edge60,Edge59,Edge58,Edge61]
  BaseFeature = -> Fillet002
  Placement = pos=(0,0,-1.5) rot=(1,0,0;3.14159rad)
  Radius = 0.2
  SupportTransform = false
  UseAllEdges = false
FEATURE [PartDesign::ShapeBinder] ReferenceFillet003
  Placement = pos=(0,0,-1.5) rot=(1,0,0;3.14159rad)
  Support = -> [Fillet003]
  TraceSupport = false
FEATURE [PartDesign::Plane] DatumPlane001
  Length = 60
  MapMode = 5
  Placement = pos=(0,-2.9e-15,6.5) rot=(0,0,1;0rad)
  ResizeMode = 0
  Support = -> [ReferenceFillet003]
  Width = 60
FEATURE [Sketcher::SketchObject] Sketch009
  ExternalGeometry = -> [ReferenceFillet003]
  FullyConstrained = true
  MapMode = 5
  Placement = pos=(0,-2.9e-15,6.5) rot=(0,0,1;0rad)
  Support = -> [DatumPlane001]
  sketch-geometry (8):
    g0: LineSegment StartX=1.4 StartY=47.5 StartZ=0 EndX=32.4 EndY=47.5 EndZ=0
    g1: LineSegment StartX=-1.6 StartY=44.5 StartZ=0 EndX=-1.6 EndY=1.5 EndZ=0
    g2: LineSegment StartX=35.4 StartY=44.5 StartZ=0 EndX=35.4 EndY=1.5 EndZ=0
    g3: LineSegment StartX=1.4 StartY=-1.5 StartZ=0 EndX=32.4 EndY=-1.5 EndZ=0
    g4: ArcOfCircle CenterX=1.4 CenterY=1.5 CenterZ=0 NormalX=0 NormalY=0 NormalZ=1 AngleXU=0 Radius=3 StartAngle=3.14159 EndAngle=4.71239
    g5: ArcOfCircle CenterX=32.4 CenterY=1.5 CenterZ=0 NormalX=0 NormalY=0 NormalZ=1 AngleXU=0 Radius=3 StartAngle=4.71239 EndAngle=6.28319
    g6: ArcOfCircle CenterX=1.4 CenterY=44.5 CenterZ=0 NormalX=0 NormalY=0 NormalZ=1 AngleXU=0 Radius=3 StartAngle=1.5708 EndAngle=3.14159
    g7: ArcOfCircle CenterX=32.4 CenterY=44.5 CenterZ=0 NormalX=0 NormalY=0 NormalZ=1 AngleXU=0 Radius=3 StartAngle=3e-16 EndAngle=1.5708
  constraints (20):
    c: Coincident(g0,g-4)
    c: Coincident(g0,g-6)
    c: Coincident(g1,g-5)
    c: Coincident(g1,g-7)
    c: Coincident(g2,g-10)
    c: Coincident(g2,g-10)
    c: Coincident(g3,g-8)
    c: Coincident(g3,g-9)
    c: Coincident(g4,g-7)
    c: Coincident(g4,g1)
    c: Coincident(g4,g3)
    c: Coincident(g5,g-9)
    c: Coincident(g5,g2)
    c: Coincident(g5,g3)
    c: Coincident(g6,g-4)
    c: Coincident(g6,g1)
    c: Coincident(g6,g0)
    c: Coincident(g7,g-6)
    c: Coincident(g7,g0)
    c: Coincident(g7,g2)
FEATURE [PartDesign::Pad] Pad004
  Direction = (0,-4e-16,1)
  Length = 4
  Length2 = 10
  Placement = pos=(0,-2.9e-15,6.5) rot=(0,0,1;0rad)
  Profile = -> Sketch009
  ReferenceAxis = -> Sketch009 [N_Axis]
  Type = 0
FEATURE [PartDesign::Fillet] Fillet004
  Base = -> Pad004 [Edge7]
  BaseFeature = -> Pad004
  Placement = pos=(0,-2.9e-15,6.5) rot=(0,0,1;0rad)
  Radius = 2.4
  SupportTransform = false
  UseAllEdges = false
FEATURE [Sketcher::SketchObject] Sketch010
  ExternalGeometry = -> [ReferenceFillet003]
  FullyConstrained = true
  MapMode = 5
  Placement = pos=(0,-2.9e-15,6.5) rot=(1,0,0;3.14159rad)
  Support = -> [Fillet004]
  sketch-geometry (8):
    g0: ArcOfCircle CenterX=2.4 CenterY=-2.5 CenterZ=0 NormalX=0 NormalY=0 NormalZ=1 AngleXU=0 Radius=2 StartAngle=1.5708 EndAngle=3.14159
    g1: ArcOfCircle CenterX=31.4 CenterY=-2.5 CenterZ=0 NormalX=0 NormalY=0 NormalZ=1 AngleXU=0 Radius=2 StartAngle=0 EndAngle=1.5708
    g2: ArcOfCircle CenterX=31.4 CenterY=-43.5 CenterZ=0 NormalX=0 NormalY=0 NormalZ=1 AngleXU=0 Radius=2 StartAngle=4.71239 EndAngle=6.28319
    g3: ArcOfCircle CenterX=2.4 CenterY=-43.5 CenterZ=0 NormalX=0 NormalY=0 NormalZ=1 AngleXU=0 Radius=2 StartAngle=3.14159 EndAngle=4.7124
    g4: LineSegment StartX=0.4 StartY=-2.5 StartZ=0 EndX=0.4 EndY=-43.5 EndZ=0
    g5: LineSegment StartX=2.4 StartY=-0.5 StartZ=0 EndX=31.4 EndY=-0.5 EndZ=0
    g6: LineSegment StartX=33.4 StartY=-2.5 StartZ=0 EndX=33.4 EndY=-43.5 EndZ=0
    g7: LineSegment StartX=31.4 StartY=-45.5 StartZ=0 EndX=2.40002 EndY=-45.5 EndZ=0
  constraints (17):
    c: Coincident(g7,g3)
    c: Vertical(g6)
    c: Horizontal(g5)
    c: Vertical(g4)
    c: Horizontal(g7)
    c: DistanceX(g-6,g3) = 1
    c: Coincident(g3,g-6)
    c: Coincident(g0,g-5)
    c: Coincident(g1,g-4)
    c: Coincident(g2,g-3)
    c: Tangent(g4,g3) = -1.5708
    c: Tangent(g4,g0) = -1.5708
    c: Tangent(g5,g0) = 1.5708
    c: Tangent(g5,g1) = 1.5708
    c: Tangent(g6,g1) = 1.5708
    c: Tangent(g6,g2) = 1.5708
    c: Tangent(g7,g2) = 1.5708
FEATURE [PartDesign::Pocket] Pocket006
  BaseFeature = -> Fillet004
  Direction = (0,-7e-16,1)
  Length = 3
  Length2 = 5
  Placement = pos=(0,-2.9e-15,6.5) rot=(0,0,1;0rad)
  Profile = -> Sketch010
  ReferenceAxis = -> Sketch010 [N_Axis]
  Type = 0
FEATURE [Sketcher::SketchObject] Sketch011
  ExternalGeometry = -> [Fillet003]
  FullyConstrained = true
  MapMode = 5
  Placement = pos=(0,-1.5,-1.5) rot=(0,0.707107,-0.707107;3.14159rad)
  Support = -> [Fillet003]
  sketch-geometry (8):
    g0: LineSegment StartX=-32.4 StartY=-8 StartZ=0 EndX=-28.9 EndY=-8 EndZ=0
    g1: LineSegment StartX=-28.9 StartY=-8 StartZ=0 EndX=-28.9 EndY=1 EndZ=0
    g2: LineSegment StartX=-28.9 StartY=1 StartZ=0 EndX=-32.4 EndY=1 EndZ=0
    g3: LineSegment StartX=-32.4 StartY=1 StartZ=0 EndX=-32.4 EndY=-8 EndZ=0
    g4: LineSegment StartX=-1.4 StartY=-8 StartZ=0 EndX=-4.9 EndY=-8 EndZ=0
    g5: LineSegment StartX=-4.9 StartY=-8 StartZ=0 EndX=-4.9 EndY=1 EndZ=0
    g6: LineSegment StartX=-4.9 StartY=1 StartZ=0 EndX=-1.4 EndY=1 EndZ=0
    g7: LineSegment StartX=-1.4 StartY=1 StartZ=0 EndX=-1.4 EndY=-8 EndZ=0
  constraints (22):
    c: Coincident(g0,g1)
    c: Coincident(g1,g2)
    c: Coincident(g2,g3)
    c: Coincident(g3,g0)
    c: Horizontal(g0)
    c: Horizontal(g2)
    c: Vertical(g1)
    c: Vertical(g3)
    c: Coincident(g0,g-3)
    c: PointOnObject(g1,g-5)
    c: Coincident(g4,g5)
    c: Coincident(g5,g6)
    c: Coincident(g6,g7)
    c: Coincident(g7,g4)
    c: Horizontal(g4)
    c: Horizontal(g6)
    c: Vertical(g5)
    c: Vertical(g7)
    c: Coincident(g4,g-4)
    c: PointOnObject(g5,g-5)
    c: DistanceX(g2,g2) = 3.5
    c: Equal(g6,g2)
FEATURE [PartDesign::Pad] Pad005
  BaseFeature = -> Fillet003
  Direction = (0,-1,-4e-16)
  Length = 5
  Length2 = 10
  Placement = pos=(0,0,-1.5) rot=(1,0,0;3.14159rad)
  Profile = -> Sketch011
  ReferenceAxis = -> Sketch011 [N_Axis]
  Type = 0
FEATURE [PartDesign::Pad] Pad006
  BaseFeature = -> Pad005
  Direction = (0,1,6e-16)
  Length = 3
  Length2 = 10
  Placement = pos=(0,0,-1.5) rot=(1,0,0;3.14159rad)
  Profile = -> Pad005 [Face18]
  Type = 0
FEATURE [PartDesign::Pad] Pad007
  BaseFeature = -> Pad006
  Direction = (0,1,7e-16)
  Length = 3
  Length2 = 10
  Placement = pos=(0,0,-1.5) rot=(1,0,0;3.14159rad)
  Profile = -> Pad006 [Face21]
  Type = 0
FEATURE [PartDesign::Fillet] Fillet005
  Base = -> Pad007 [Edge78,Edge70,Edge166,Edge161]
  BaseFeature = -> Pad007
  Placement = pos=(0,0,-1.5) rot=(1,0,0;3.14159rad)
  Radius = 3
  SupportTransform = false
  UseAllEdges = false
FEATURE [Sketcher::SketchObject] Sketch012
  ExternalGeometry = -> [Fillet005]
  FullyConstrained = true
  MapMode = 5
  Placement = pos=(0,47.5,-1.5) rot=(-1,0,0;1.5708rad)
  Support = -> [Fillet005]
  sketch-geometry (8):
    g0: LineSegment StartX=1.4 StartY=-8 StartZ=0 EndX=4.9 EndY=-8 EndZ=0
    g1: LineSegment StartX=4.9 StartY=-8 StartZ=0 EndX=4.9 EndY=1 EndZ=0
    g2: LineSegment StartX=4.9 StartY=1 StartZ=0 EndX=1.4 EndY=1 EndZ=0
    g3: LineSegment StartX=1.4 StartY=1 StartZ=0 EndX=1.4 EndY=-8 EndZ=0
    g4: LineSegment StartX=32.4 StartY=-8 StartZ=0 EndX=28.9 EndY=-8 EndZ=0
    g5: LineSegment StartX=28.9 StartY=-8 StartZ=0 EndX=28.9 EndY=1 EndZ=0
    g6: LineSegment StartX=28.9 StartY=1 StartZ=0 EndX=32.4 EndY=1 EndZ=0
    g7: LineSegment StartX=32.4 StartY=1 StartZ=0 EndX=32.4 EndY=-8 EndZ=0
  constraints (22):
    c: Coincident(g0,g1)
    c: Coincident(g1,g2)
    c: Coincident(g2,g3)
    c: Coincident(g3,g0)
    c: Horizontal(g0)
    c: Horizontal(g2)
    c: Vertical(g1)
    c: Vertical(g3)
    c: Coincident(g0,g-4)
    c: PointOnObject(g1,g-3)
    c: Coincident(g4,g5)
    c: Coincident(g5,g6)
    c: Coincident(g6,g7)
    c: Coincident(g7,g4)
    c: Horizontal(g4)
    c: Horizontal(g6)
    c: Vertical(g5)
    c: Vertical(g7)
    c: Coincident(g4,g-5)
    c: PointOnObject(g5,g-3)
    c: DistanceX(g2,g2) = 3.5
    c: Equal(g6,g2)
FEATURE [PartDesign::Pad] Pad008
  BaseFeature = -> Fillet005
  Direction = (0,1,7e-16)
  Length = 5
  Length2 = 10
  Placement = pos=(0,0,-1.5) rot=(1,0,0;3.14159rad)
  Profile = -> Sketch012
  ReferenceAxis = -> Sketch012 [N_Axis]
  Type = 0
FEATURE [PartDesign::Pad] Pad009
  BaseFeature = -> Pad008
  Direction = (0,-1,-9e-16)
  Length = 3
  Length2 = 10
  Placement = pos=(0,0,-1.5) rot=(1,0,0;3.14159rad)
  Profile = -> Pad008 [Face68,Face67]
  Type = 0
FEATURE [PartDesign::Fillet] Fillet006
  Base = -> Pad009 [Edge247,Edge241,Edge143,Edge148]
  BaseFeature = -> Pad009
  Placement = pos=(0,0,-1.5) rot=(1,0,0;3.14159rad)
  Radius = 3
  SupportTransform = false
  UseAllEdges = false
FEATURE [PartDesign::Fillet] Fillet007
  Base = -> Fillet006 [Edge234,Edge247,Edge246,Edge244,Edge242,Edge213,Edge218,Edge217,Edge215,Edge226,Edge221,Edge225,Edge223,Edge239,Edge238,Edge236,Edge230,Edge228,Edge231,Edge229]
  BaseFeature = -> Fillet006
  Placement = pos=(0,0,-1.5) rot=(1,0,0;3.14159rad)
  Radius = 0.8
  SupportTransform = false
  UseAllEdges = false
FEATURE [Sketcher::SketchObject] Sketch014
  ExternalGeometry = -> [Fillet007]
  FullyConstrained = true
  MapMode = 5
  Placement = pos=(32.4,0,-1.5) rot=(0.57735,-0.57735,0.57735;4.18879rad)
  Support = -> [Fillet007]
  sketch-geometry (2):
    g0: Circle CenterX=4 CenterY=-3.5 CenterZ=0 NormalX=0 NormalY=0 NormalZ=1 AngleXU=0 Radius=0.6
    g1: Circle CenterX=-50 CenterY=-3.5 CenterZ=0 NormalX=0 NormalY=0 NormalZ=1 AngleXU=0 Radius=0.6
  constraints (6):
    c: Diameter(g0) = 1.2
    c: Equal(g1,g0)
    c: DistanceY(g0,g-3) = 1.5
    c: DistanceX(g0,g-3) = 2.5
    c: DistanceY(g1,g-4) = 1.5
    c: DistanceX(g-4,g1) = 2.5
FEATURE [PartDesign::Pocket] Pocket007
  BaseFeature = -> Fillet007
  Direction = (-1,0,0)
  Length = 5
  Length2 = 5
  Placement = pos=(0,0,-1.5) rot=(1,0,0;3.14159rad)
  Profile = -> Sketch014
  ReferenceAxis = -> Sketch014 [N_Axis]
  Type = 1
FEATURE [PartDesign::Pad] Pad010
  BaseFeature = -> Pocket007
  Direction = (0,-1.4e-15,1)
  Length = 1
  Length2 = 10
  Placement = pos=(0,0,-1.5) rot=(1,0,0;3.14159rad)
  Profile = -> Pocket007 [Face64]
  Type = 0
FEATURE [Sketcher::SketchObject] Sketch015
  ExternalGeometry = -> [Pad010]
  FullyConstrained = true
  MapMode = 5
  Placement = pos=(0,-1e-15,0.5) rot=(0,0,1;0rad)
  sketch-geometry (4):
    g0: LineSegment StartX=0.48 StartY=9.57 StartZ=0 EndX=33.31 EndY=9.57 EndZ=0
    g1: LineSegment StartX=33.31 StartY=9.57 StartZ=0 EndX=33.31 EndY=3.87 EndZ=0
    g2: LineSegment StartX=33.31 StartY=3.87 StartZ=0 EndX=0.48 EndY=3.87 EndZ=0
    g3: LineSegment StartX=0.48 StartY=3.87 StartZ=0 EndX=0.48 EndY=9.57 EndZ=0
  constraints (10):
    c: Coincident(g0,g1)
    c: Coincident(g1,g2)
    c: Coincident(g2,g3)
    c: Coincident(g3,g0)
    c: Horizontal(g2)
    c: Vertical(g1)
    c: Vertical(g3)
    c: Coincident(g0,g-3)
    c: DistanceY(g3,g3) = 5.7
    c: Coincident(g0,g-3)
FEATURE [PartDesign::Pocket] Pocket008
  BaseFeature = -> Pad010
  Direction = (0,0,-1)
  Length = 1.52
  Length2 = 5
  Placement = pos=(0,0,-1.5) rot=(1,0,0;3.14159rad)
  Profile = -> Sketch015
  ReferenceAxis = -> Sketch015 [N_Axis]
  Type = 0
FEATURE [PartDesign::ShapeBinder] ShapeBinder
  Support = -> [Part__Feature055]
  TraceSupport = false
FEATURE [Sketcher::SketchObject] Sketch016
  ExternalGeometry = -> [ShapeBinder]
  FullyConstrained = true
  MapMode = 5
  Placement = pos=(0,-1e-15,0.5) rot=(0,0,1;0rad)
  sketch-geometry (8):
    g0: ArcOfCircle CenterX=3.9 CenterY=42.96 CenterZ=0 NormalX=0 NormalY=0 NormalZ=1 AngleXU=0 Radius=0.8 StartAngle=1.5708 EndAngle=4.71239
    g1: ArcOfCircle CenterX=29.9 CenterY=42.96 CenterZ=0 NormalX=0 NormalY=0 NormalZ=1 AngleXU=0 Radius=0.8 StartAngle=4.71239 EndAngle=7.85398
    g2: LineSegment StartX=3.9 StartY=43.76 StartZ=0 EndX=29.9 EndY=43.76 EndZ=0
    g3: LineSegment StartX=29.9 StartY=42.16 StartZ=0 EndX=3.9 EndY=42.16 EndZ=0
    g4: ArcOfCircle CenterX=3.9 CenterY=3 CenterZ=0 NormalX=0 NormalY=0 NormalZ=1 AngleXU=0 Radius=0.8 StartAngle=1.5708 EndAngle=4.71239
    g5: ArcOfCircle CenterX=29.9 CenterY=3 CenterZ=0 NormalX=0 NormalY=0 NormalZ=1 AngleXU=0 Radius=0.8 StartAngle=4.71239 EndAngle=7.85398
    g6: LineSegment StartX=3.9 StartY=3.8 StartZ=0 EndX=29.9 EndY=3.8 EndZ=0
    g7: LineSegment StartX=29.9 StartY=2.2 StartZ=0 EndX=3.9 EndY=2.2 EndZ=0
  constraints (18):
    c: Coincident(g0,g-5)
    c: Diameter(g0) = 1.6
    c: Coincident(g1,g-6)
    c: Equal(g0,g1)
    c: Coincident(g2,g1)
    c: Horizontal(g2)
    c: Coincident(g3,g1)
    c: Horizontal(g3)
    c: Tangent(g3,g0) = 1.5708
    c: Tangent(g2,g0) = 1.5708
    c: Coincident(g4,g-8)
    c: Coincident(g5,g-10)
    c: Equal(g4,g5)
    c: Tangent(g7,g4) = 1.5708
    c: Tangent(g6,g4) = 1.5708
    c: Tangent(g6,g5) = 1.5708
    c: Tangent(g7,g5) = 1.5708
    c: Equal(g4,g0)
FEATURE [PartDesign::Pad] Pad011
  BaseFeature = -> Pocket008
  Direction = (0,-1e-15,1)
  Length = 4
  Length2 = 10
  Placement = pos=(0,0,-1.5) rot=(1,0,0;3.14159rad)
  Profile = -> Sketch016
  ReferenceAxis = -> Sketch016 [N_Axis]
  Type = 0
FEATURE [PartDesign::ShapeBinder] ShapeBinder001
  Support = -> [Pad011]
  TraceSupport = false
FEATURE [Sketcher::SketchObject] Sketch020
  FullyConstrained = false
  MapMode = 5
  Placement = pos=(0,-1.2e-14,4.5) rot=(0,0,1;0rad)
  sketch-geometry (6):
    g0: Circle CenterX=5.9 CenterY=42.96 CenterZ=0 NormalX=0 NormalY=0 NormalZ=1 AngleXU=0 Radius=0.9
    g1: Circle CenterX=27.9 CenterY=42.96 CenterZ=0 NormalX=0 NormalY=0 NormalZ=1 AngleXU=0 Radius=0.9
    g2: Circle CenterX=5.9 CenterY=3 CenterZ=0 NormalX=0 NormalY=0 NormalZ=1 AngleXU=0 Radius=0.9
    g3: Circle CenterX=27.9 CenterY=3 CenterZ=0 NormalX=0 NormalY=0 NormalZ=1 AngleXU=0 Radius=0.9
    g4: LineSegment StartX=3.9 StartY=3 StartZ=0 EndX=29.9 EndY=3 EndZ=0
    g5: LineSegment StartX=3.9 StartY=42.96 StartZ=0 EndX=29.9 EndY=42.96 EndZ=0
  constraints (12):
    c: PointOnObject(g1,g5)
    c: PointOnObject(g0,g5)
    c: PointOnObject(g2,g4)
    c: PointOnObject(g3,g4)
    c: DistanceX(g5,g0) = 2
    c: DistanceX(g1,g5) = 2
    c: DistanceX(g4,g2) = 2
    c: DistanceX(g3,g4) = 2
    c: Diameter(g0) = 1.8
    c: Equal(g0,g1)
    c: Equal(g1,g3)
    c: Equal(g3,g2)
FEATURE [PartDesign::Pocket] Pocket011
  BaseFeature = -> Pad011
  Direction = (0,2e-15,-1)
  Length = 3
  Length2 = 5
  Placement = pos=(0,0,-1.5) rot=(1,0,0;3.14159rad)
  Profile = -> Sketch020
  ReferenceAxis = -> Sketch020 [N_Axis]
  Type = 0
FEATURE [Sketcher::SketchObject] Sketch021
  FullyConstrained = false
  MapMode = 5
  Placement = pos=(0,-8e-15,6.5) rot=(1,0,0;3.14159rad)
  sketch-geometry (16):
    g0: ArcOfCircle CenterX=2.4 CenterY=-2.5 CenterZ=0 NormalX=0 NormalY=0 NormalZ=1 AngleXU=0 Radius=2.65 StartAngle=1.5708 EndAngle=3.1416
    g1: LineSegment StartX=2.4 StartY=0.15 StartZ=0 EndX=31.4 EndY=0.15 EndZ=0
    g2: ArcOfCircle CenterX=31.4 CenterY=-2.5 CenterZ=0 NormalX=0 NormalY=0 NormalZ=1 AngleXU=0 Radius=2.65 StartAngle=0 EndAngle=1.5708
    g3: LineSegment StartX=34.05 StartY=-2.5 StartZ=0 EndX=34.05 EndY=-43.5 EndZ=0
    g4: ArcOfCircle CenterX=31.4 CenterY=-43.5 CenterZ=0 NormalX=0 NormalY=0 NormalZ=1 AngleXU=0 Radius=2.65 StartAngle=4.71239 EndAngle=6.28319
    g5: LineSegment StartX=31.4 StartY=-46.15 StartZ=0 EndX=2.4 EndY=-46.15 EndZ=0
    g6: ArcOfCircle CenterX=2.4 CenterY=-43.5 CenterZ=0 NormalX=0 NormalY=0 NormalZ=1 AngleXU=0 Radius=2.65 StartAngle=3.14159 EndAngle=4.71239
    g7: LineSegment StartX=-0.25 StartY=-43.5 StartZ=0 EndX=-0.25 EndY=-2.50001 EndZ=0
    g8: ArcOfCircle CenterX=2.4 CenterY=-2.5 CenterZ=0 NormalX=0 NormalY=0 NormalZ=1 AngleXU=0 Radius=2 StartAngle=1.5708 EndAngle=3.14159
    g9: ArcOfCircle CenterX=31.4 CenterY=-2.5 CenterZ=0 NormalX=0 NormalY=0 NormalZ=1 AngleXU=0 Radius=2 StartAngle=0 EndAngle=1.5708
    g10: ArcOfCircle CenterX=31.4 CenterY=-43.5 CenterZ=0 NormalX=0 NormalY=0 NormalZ=1 AngleXU=0 Radius=2 StartAngle=4.71239 EndAngle=6.28319
    g11: ArcOfCircle CenterX=2.4 CenterY=-43.5 CenterZ=0 NormalX=0 NormalY=0 NormalZ=1 AngleXU=0 Radius=2 StartAngle=3.14159 EndAngle=4.71239
    g12: LineSegment StartX=2.4 StartY=-0.5 StartZ=0 EndX=31.4 EndY=-0.5 EndZ=0
    g13: LineSegment StartX=33.4 StartY=-2.5 StartZ=0 EndX=33.4 EndY=-43.5 EndZ=0
    g14: LineSegment StartX=31.4 StartY=-45.5 StartZ=0 EndX=2.4 EndY=-45.5 EndZ=0
    g15: LineSegment StartX=0.4 StartY=-43.5 StartZ=0 EndX=0.4 EndY=-2.5 EndZ=0
  constraints (27):
    c: Vertical(g3)
    c: Horizontal(g5)
    c: Coincident(g7,g0)
    c: Vertical(g7)
    c: Tangent(g1,g0) = 1.5708
    c: Tangent(g2,g1) = 1.5708
    c: Tangent(g3,g2) = 1.5708
    c: Tangent(g4,g3) = 1.5708
    c: Tangent(g5,g4) = 1.5708
    c: Tangent(g6,g5) = 1.5708
    c: Tangent(g7,g6) = 1.5708
    c: Coincident(g8,g0)
    c: Coincident(g9,g2)
    c: Coincident(g10,g4)
    c: Coincident(g11,g6)
    c: Coincident(g12,g8)
    c: Coincident(g12,g9)
    c: Horizontal(g12)
    c: Vertical(g13)
    c: Horizontal(g14)
    c: Vertical(g15)
    c: Tangent(g15,g8) = 1.5708
    c: Tangent(g15,g11) = 1.5708
    c: Tangent(g14,g11) = 1.5708
    c: Tangent(g14,g10) = 1.5708
    c: Tangent(g13,g10) = 1.5708
    c: Tangent(g13,g9) = 1.5708
FEATURE [PartDesign::Pad] Pad013
  BaseFeature = -> Pocket006
  Direction = (0,4e-15,-1)
  Length = 1
  Length2 = 10
  Placement = pos=(0,-2.9e-15,6.5) rot=(0,0,1;0rad)
  Profile = -> Sketch021
  ReferenceAxis = -> Sketch021 [N_Axis]
  Type = 0
FEATURE [Sketcher::SketchObject] Sketch022
  ExternalGeometry = -> [Pad013]
  FullyConstrained = true
  MapMode = 5
  Placement = pos=(0,-7.4e-15,9.5) rot=(1,0,0;3.14159rad)
  Support = -> [Pad013]
  sketch-geometry (9):
    g0: GeomPoint X=16.9 Y=-23 Z=0
    g1: LineSegment StartX=2.9 StartY=-10 StartZ=0 EndX=30.9 EndY=-10 EndZ=0
    g2: LineSegment StartX=30.9 StartY=-10 StartZ=0 EndX=30.9 EndY=-13 EndZ=0
    g3: LineSegment StartX=30.9 StartY=-13 StartZ=0 EndX=2.9 EndY=-13 EndZ=0
    g4: LineSegment StartX=2.9 StartY=-13 StartZ=0 EndX=2.9 EndY=-10 EndZ=0
    g5: LineSegment StartX=2.9 StartY=-33 StartZ=0 EndX=30.9 EndY=-33 EndZ=0
    g6: LineSegment StartX=30.9 StartY=-33 StartZ=0 EndX=30.9 EndY=-36 EndZ=0
    g7: LineSegment StartX=30.9 StartY=-36 StartZ=0 EndX=2.9 EndY=-36 EndZ=0
    g8: LineSegment StartX=2.9 StartY=-36 StartZ=0 EndX=2.9 EndY=-33 EndZ=0
  constraints (23):
    c: Coincident(g1,g2)
    c: Coincident(g2,g3)
    c: Coincident(g3,g4)
    c: Coincident(g4,g1)
    c: Horizontal(g1)
    c: Horizontal(g3)
    c: Vertical(g2)
    c: Vertical(g4)
    c: Coincident(g5,g6)
    c: Coincident(g6,g7)
    c: Coincident(g7,g8)
    c: Coincident(g8,g5)
    c: Horizontal(g7)
    c: Vertical(g6)
    c: Vertical(g8)
    c: DistanceX(g1,g1) = 28
    c: DistanceY(g2,g2) = 3
    c: Equal(g2,g6)
    c: Symmetric(g5,g2,g0)
    c: Symmetric(g5,g3,g0)
    c: DistanceX(g5,g3) = 0
    c: DistanceY(g5,g2) = 20
    c: Symmetric(g-3,g-4,g0)
FEATURE [PartDesign::Pad] Pad014
  BaseFeature = -> Pad013
  Direction = (0,1.5e-15,-1)
  Length = 3
  Length2 = 10
  Placement = pos=(0,-2.9e-15,6.5) rot=(0,0,1;0rad)
  Profile = -> Sketch022
  ReferenceAxis = -> Sketch022 [N_Axis]
  Type = 0
FEATURE [Sketcher::SketchObject] Sketch023
  ExternalGeometry = -> [Pad014]
  FullyConstrained = true
  MapMode = 5
  Placement = pos=(0,-8.5e-15,9.5) rot=(1,0,0;3.14159rad)
  Support = -> [Pad014]
  sketch-geometry (12):
    g0: ArcOfCircle CenterX=2.4 CenterY=-43.5 CenterZ=0 NormalX=0 NormalY=0 NormalZ=1 AngleXU=0 Radius=2 StartAngle=3.14159 EndAngle=4.71239
    g1: ArcOfCircle CenterX=31.4 CenterY=-43.5 CenterZ=0 NormalX=0 NormalY=0 NormalZ=1 AngleXU=0 Radius=2 StartAngle=4.71239 EndAngle=6.28319
    g2: ArcOfCircle CenterX=2.4 CenterY=-2.5 CenterZ=0 NormalX=0 NormalY=0 NormalZ=1 AngleXU=0 Radius=2 StartAngle=1.5708 EndAngle=3.14159
    g3: ArcOfCircle CenterX=31.4 CenterY=-2.5 CenterZ=0 NormalX=0 NormalY=0 NormalZ=1 AngleXU=0 Radius=2 StartAngle=0 EndAngle=1.5708
    g4: LineSegment StartX=2.4 StartY=-0.5 StartZ=0 EndX=31.4 EndY=-0.5 EndZ=0
    g5: LineSegment StartX=2.4 StartY=-45.5 StartZ=0 EndX=31.4 EndY=-45.5 EndZ=0
    g6: LineSegment StartX=0.4 StartY=-43.5 StartZ=0 EndX=0.4 EndY=-39.7 EndZ=0
    g7: LineSegment StartX=0.4 StartY=-39.7 StartZ=0 EndX=33.4 EndY=-39.7 EndZ=0
    g8: LineSegment StartX=33.4 StartY=-39.7 StartZ=0 EndX=33.4 EndY=-43.5 EndZ=0
    g9: LineSegment StartX=0.4 StartY=-2.5 StartZ=0 EndX=0.4 EndY=-6.3 EndZ=0
    g10: LineSegment StartX=0.4 StartY=-6.3 StartZ=0 EndX=33.4 EndY=-6.3 EndZ=0
    g11: LineSegment StartX=33.4 StartY=-6.3 StartZ=0 EndX=33.4 EndY=-2.5 EndZ=0
  constraints (32):
    c: Coincident(g0,g-6)
    c: Coincident(g0,g-6)
    c: Coincident(g0,g-7)
    c: Coincident(g1,g-8)
    c: Coincident(g1,g-8)
    c: Coincident(g1,g-8)
    c: Coincident(g2,g-5)
    c: Coincident(g2,g-5)
    c: Coincident(g2,g-5)
    c: Coincident(g3,g-3)
    c: Coincident(g3,g-4)
    c: Coincident(g3,g-3)
    c: Coincident(g4,g2)
    c: Coincident(g4,g3)
    c: Coincident(g5,g0)
    c: Coincident(g5,g1)
    c: Coincident(g6,g0)
    c: Vertical(g6)
    c: Coincident(g7,g6)
    c: Horizontal(g7)
    c: Coincident(g8,g7)
    c: Coincident(g8,g1)
    c: Vertical(g8)
    c: DistanceY(g8,g8) = 3.8
    c: Coincident(g9,g2)
    c: Vertical(g9)
    c: Coincident(g10,g9)
    c: Horizontal(g10)
    c: Coincident(g11,g10)
    c: Coincident(g11,g3)
    c: Vertical(g11)
    c: Equal(g11,g8)
FEATURE [PartDesign::Pad] Pad015
  BaseFeature = -> Pad014
  Direction = (0,1.8e-15,-1)
  Length = 4
  Length2 = 10
  Placement = pos=(0,-2.9e-15,6.5) rot=(0,0,1;0rad)
  Profile = -> Sketch023
  ReferenceAxis = -> Sketch023 [N_Axis]
  Type = 0
FEATURE [Sketcher::SketchObject] Sketch024
  ExternalGeometry = -> [ShapeBinder001]
  FullyConstrained = true
  MapMode = 5
  Placement = pos=(0,-8e-16,5.5) rot=(1,0,0;3.14159rad)
  Support = -> [Pad015]
  sketch-geometry (6):
    g0: Circle CenterX=5.9 CenterY=-42.96 CenterZ=0 NormalX=0 NormalY=0 NormalZ=1 AngleXU=0 Radius=1
    g1: Circle CenterX=27.9 CenterY=-42.96 CenterZ=0 NormalX=0 NormalY=0 NormalZ=1 AngleXU=0 Radius=1
    g2: Circle CenterX=5.9 CenterY=-3 CenterZ=0 NormalX=0 NormalY=0 NormalZ=1 AngleXU=0 Radius=1
    g3: Circle CenterX=27.9 CenterY=-3 CenterZ=0 NormalX=0 NormalY=0 NormalZ=1 AngleXU=0 Radius=1
    g4: LineSegment StartX=3.9 StartY=-42.96 StartZ=0 EndX=29.9 EndY=-42.96 EndZ=0
    g5: LineSegment StartX=3.9 StartY=-3 StartZ=0 EndX=29.9 EndY=-3 EndZ=0
  constraints (16):
    c: PointOnObject(g3,g5)
    c: PointOnObject(g2,g5)
    c: PointOnObject(g0,g4)
    c: PointOnObject(g1,g4)
    c: Diameter(g0) = 2
    c: Equal(g1,g0)
    c: Equal(g0,g2)
    c: Equal(g2,g3)
    c: DistanceX(g5,g2) = 2
    c: DistanceX(g3,g5) = 2
    c: DistanceX(g4,g0) = 2
    c: DistanceX(g1,g4) = 2
    c: Coincident(g5,g-3)
    c: Coincident(g5,g-4)
    c: Coincident(g4,g-5)
    c: Coincident(g4,g-6)
FEATURE [PartDesign::Pocket] Pocket012
  BaseFeature = -> Pad015
  Direction = (0,-2.2e-15,1)
  Length = 5
  Length2 = 5
  Placement = pos=(0,-2.9e-15,6.5) rot=(0,0,1;0rad)
  Profile = -> Sketch024
  ReferenceAxis = -> Sketch024 [N_Axis]
  Type = 1
FEATURE [Sketcher::SketchObject] Sketch025
  ExternalGeometry = -> [Pocket012]
  FullyConstrained = true
  MapMode = 5
  Placement = pos=(0,-1.32e-14,10.5) rot=(0,0,1;0rad)
  Support = -> [Pocket012]
  sketch-geometry (4):
    g0: Circle CenterX=5.9 CenterY=42.96 CenterZ=0 NormalX=0 NormalY=0 NormalZ=1 AngleXU=0 Radius=2.125
    g1: Circle CenterX=27.9 CenterY=42.96 CenterZ=0 NormalX=0 NormalY=0 NormalZ=1 AngleXU=0 Radius=2.125
    g2: Circle CenterX=5.9 CenterY=3 CenterZ=0 NormalX=0 NormalY=0 NormalZ=1 AngleXU=0 Radius=2.125
    g3: Circle CenterX=27.9 CenterY=3 CenterZ=0 NormalX=0 NormalY=0 NormalZ=1 AngleXU=0 Radius=2.125
  constraints (8):
    c: Coincident(g0,g-3)
    c: Coincident(g1,g-4)
    c: Coincident(g2,g-5)
    c: Coincident(g3,g-6)
    c: Diameter(g0) = 4.25
    c: Equal(g0,g1)
    c: Equal(g1,g3)
    c: Equal(g3,g2)
FEATURE [PartDesign::Pocket] Pocket013
  BaseFeature = -> Pocket012
  Direction = (0,2.6e-15,-1)
  Length = 3
  Length2 = 5
  Placement = pos=(0,-2.9e-15,6.5) rot=(0,0,1;0rad)
  Profile = -> Sketch025
  ReferenceAxis = -> Sketch025 [N_Axis]
  Type = 0
FEATURE [PartDesign::Fillet] Fillet009
  Base = -> Pocket013 [Edge136,Edge132,Edge131,Edge134,Edge139,Edge142,Edge140,Edge144]
  BaseFeature = -> Pocket013
  Placement = pos=(0,-2.9e-15,6.5) rot=(0,0,1;0rad)
  Radius = 1
  SupportTransform = false
  UseAllEdges = false
FEATURE [PartDesign::Body] Body002  label="Case_Bottom"
  Group = -> [DatumPlane001,ReferenceFillet003,Sketch009,Pad004,Fillet004,Sketch010,Pocket006,ShapeBinder001,Sketch021,Pad013,Sketch022,Pad014,Sketch023,Pad015,Sketch024,Pocket012,Sketch025,Pocket013,Fillet009]
  Origin = -> Origin115
  Tip = -> Fillet009
FEATURE [PartDesign::Pad] Pad016
  BaseFeature = -> Pocket011
  Direction = (0,-1.8e-15,1)
  Length = 0.4
  Length2 = 10
  Placement = pos=(0,0,-1.5) rot=(1,0,0;3.14159rad)
  Profile = -> Pocket011 [Face66]
  Type = 0
FEATURE [PartDesign::Pad] Pad018
  BaseFeature = -> Pad016
  Direction = (0,-1.4e-15,1)
  Length = 0.5
  Length2 = 10
  Placement = pos=(0,0,-1.5) rot=(1,0,0;3.14159rad)
  Profile = -> Pad016 [Face169,Face173,Face177,Face180,Face184,Face188]
  Type = 0
FEATURE [Part::Part2DObjectPython] ShapeString  # Draft 2D object (typed FeaturePython)
  FontFile = <userpath>/Téléchargements/ubuntu/Ubuntu-B.ttf
  MakeFace = true
  Placement = pos=(28.3629,3.34221,-2.5) rot=(0,1,0;3.14159rad)
  Size = 2.5
  String = Watchy
  Tracking = 0
FEATURE [Part::Extrusion] Extrude  label="Watchy"
  Base = -> ShapeString
  Dir = (0,0,-1)
  DirMode = 2
  FaceMakerClass = Part::FaceMakerBullseye
  LengthFwd = 0.5
  LengthRev = 0
  Placement = pos=(0.184744,0.772381,0.5) rot=(0,0,1;0rad)
  Solid = false
  Symmetric = false
FEATURE [PartDesign::ShapeBinder] ReferencePart__Feature055
  Support = -> [Part__Feature055]
  TraceSupport = false
FEATURE [PartDesign::Plane] DatumPlane002
  Length = 70.0989
  MapMode = 5
  Placement = pos=(0,0,1.6) rot=(0,0,1;0rad)
  ResizeMode = 0
  Support = -> [ReferencePart__Feature055]
  Width = 83.1771
FEATURE [Sketcher::SketchObject] Sketch026
  ExternalGeometry = -> [ReferencePart__Feature055]
  FullyConstrained = true
  MapMode = 5
  Placement = pos=(0,0,1.6) rot=(0,0,1;0rad)
  Support = -> [DatumPlane002]
  sketch-geometry (8):
    g0: ArcOfCircle CenterX=3.9 CenterY=42.96 CenterZ=0 NormalX=0 NormalY=0 NormalZ=1 AngleXU=0 Radius=1 StartAngle=1.5708 EndAngle=4.71239
    g1: ArcOfCircle CenterX=29.9 CenterY=42.96 CenterZ=0 NormalX=0 NormalY=0 NormalZ=1 AngleXU=0 Radius=1 StartAngle=4.71239 EndAngle=7.85398
    g2: LineSegment StartX=3.9 StartY=43.96 StartZ=0 EndX=29.9 EndY=43.96 EndZ=0
    g3: LineSegment StartX=29.9 StartY=41.96 StartZ=0 EndX=3.9 EndY=41.96 EndZ=0
    g4: ArcOfCircle CenterX=3.9 CenterY=42.96 CenterZ=0 NormalX=0 NormalY=0 NormalZ=1 AngleXU=0 Radius=2.5 StartAngle=1.5708 EndAngle=4.71239
    g5: ArcOfCircle CenterX=29.9 CenterY=42.96 CenterZ=0 NormalX=0 NormalY=0 NormalZ=1 AngleXU=0 Radius=2.5 StartAngle=4.71239 EndAngle=7.85398
    g6: LineSegment StartX=3.9 StartY=45.46 StartZ=0 EndX=29.9 EndY=45.46 EndZ=0
    g7: LineSegment StartX=3.9 StartY=40.46 StartZ=0 EndX=29.9 EndY=40.46 EndZ=0
  constraints (19):
    c: Coincident(g0,g-4)
    c: Coincident(g0,g-4)
    c: Coincident(g0,g-5)
    c: Coincident(g1,g-6)
    c: Coincident(g1,g-6)
    c: Coincident(g1,g-6)
    c: Coincident(g2,g0)
    c: Coincident(g2,g1)
    c: Coincident(g3,g1)
    c: Coincident(g3,g0)
    c: Coincident(g5,g1)
    c: Horizontal(g6)
    c: Horizontal(g7)
    c: DistanceY(g0,g4) = 1.5
    c: Tangent(g6,g4) = 1.5708
    c: Tangent(g6,g5) = 1.5708
    c: Tangent(g7,g5) = -1.5708
    c: Tangent(g7,g4) = -1.5708
    c: Coincident(g0,g4)
FEATURE [PartDesign::Pad] Pad019
  Direction = (0,0,1)
  Length = 3.5
  Length2 = 10
  Placement = pos=(0,0,1.6) rot=(0,0,1;0rad)
  Profile = -> Sketch026
  ReferenceAxis = -> Sketch026 [N_Axis]
  Type = 0
FEATURE [PartDesign::Body] Body003  label="Bride"
  Group = -> [DatumPlane002,ReferencePart__Feature055,Sketch026,Pad019]
  Origin = -> Origin116
  Tip = -> Pad019
FEATURE [PartDesign::FeatureBase] Clone
  BaseFeature = -> Body003
FEATURE [PartDesign::Body] Body004  label="Bride2"
  BaseFeature = -> Body003
  Group = -> [Clone]
  Origin = -> Origin117
  Placement = pos=(0,-40,0) rot=(0,0,1;0rad)
  Tip = -> Clone
FEATURE [Mesh::Feature] Micro_USB_Cover
  Placement = pos=(36.4,26.7,5) rot=(0.707107,-0.707107,0;3.14159rad)
FEATURE [Part::Feature] Micro_USB_Cover001
  shape: bbox 6 x 8.5 x 3.5 mm, 1068 faces, 0 solids (baked)
FEATURE [Sketcher::SketchObject] Sketch027
  FullyConstrained = true
  MapMode = 5
  Placement = pos=(0,0,0) rot=(0.57735,0.57735,0.57735;2.0944rad)
  Support = -> [YZ_Plane118]
  sketch-geometry (4):
    g0: LineSegment StartX=17.7 StartY=5.55 StartZ=0 EndX=27.2 EndY=5.55 EndZ=0
    g1: LineSegment StartX=27.2 StartY=5.55 StartZ=0 EndX=27.2 EndY=0.95 EndZ=0
    g2: LineSegment StartX=27.2 StartY=0.95 StartZ=0 EndX=17.7 EndY=0.95 EndZ=0
    g3: LineSegment StartX=17.7 StartY=0.95 StartZ=0 EndX=17.7 EndY=5.55 EndZ=0
  constraints (12):
    c: Coincident(g0,g1)
    c: Coincident(g1,g2)
    c: Coincident(g2,g3)
    c: Coincident(g3,g0)
    c: Horizontal(g0)
    c: Horizontal(g2)
    c: Vertical(g1)
    c: Vertical(g3)
    c: DistanceX(g0,g0) = 9.5
    c: DistanceY(g1,g1) = 4.6
    c: DistanceY(g-1,g2) = 0.95
    c: DistanceX(g-1,g2) = 17.7
FEATURE [PartDesign::Pad] Pad020
  Direction = (1,-2e-16,3e-16)
  Length = 2
  Length2 = 10
  Placement = pos=(0,0,0) rot=(0.57735,0.57735,0.57735;2.0944rad)
  Profile = -> Sketch027
  ReferenceAxis = -> Sketch027 [N_Axis]
  Type = 0
FEATURE [Part::Feature] Micro_USB_Cover001_solid  label="Micro_USB_Cover001 (Solid)"
  Placement = pos=(0.5,0,0) rot=(0,0,1;0rad)
  shape: bbox 6 x 8.5 x 3.5 mm, 1068 faces (baked)
FEATURE [PartDesign::ShapeBinder] ShapeBinder002
  Support = -> [Micro_USB_Cover001_solid]
  TraceSupport = false
FEATURE [PartDesign::Fillet] Fillet010
  Base = -> Pad020 [Edge1,Edge8,Edge5,Edge2,Edge4,Edge7,Edge10,Edge12]
  BaseFeature = -> Pad020
  Placement = pos=(0,0,0) rot=(0.57735,0.57735,0.57735;2.0944rad)
  Radius = 1
  SupportTransform = false
  UseAllEdges = false
FEATURE [PartDesign::Body] Body005
  Group = -> [Sketch027,Pad020,ShapeBinder002,Fillet010]
  Origin = -> Origin118
  Placement = pos=(35.4,0,0) rot=(0,0,1;0rad)
  Tip = -> Fillet010
FEATURE [Part::Fuse] Fusion  label="USB_Cap"
  Base = -> Body005
  Tool = -> Micro_USB_Cover001_solid
FEATURE [PartDesign::ShapeBinder] ShapeBinder003
  Placement = pos=(0,0,-2.5) rot=(1,0,0;3.14159rad)
  Support = -> [Sketch002]
  TraceSupport = false
FEATURE [Sketcher::SketchObject] Sketch028
  ExternalGeometry = -> [ShapeBinder003]
  FullyConstrained = true
  MapMode = 5
  Placement = pos=(0,0,-1.5) rot=(1,0,0;3.14159rad)
  Support = -> [Pocket]
  sketch-geometry (4):
    g0: LineSegment StartX=3 StartY=-12.3 StartZ=0 EndX=31 EndY=-12.3 EndZ=0
    g1: LineSegment StartX=31 StartY=-39.3 StartZ=0 EndX=31 EndY=-12.3 EndZ=0
    g2: LineSegment StartX=31 StartY=-39.3 StartZ=0 EndX=3 EndY=-39.3 EndZ=0
    g3: LineSegment StartX=3 StartY=-12.3 StartZ=0 EndX=3 EndY=-39.3 EndZ=0
  constraints (8):
    c: Coincident(g0,g-3)
    c: Coincident(g0,g-4)
    c: Coincident(g1,g-5)
    c: Coincident(g1,g0)
    c: Coincident(g2,g1)
    c: Coincident(g2,g-5)
    c: Coincident(g3,g0)
    c: Coincident(g3,g2)
FEATURE [PartDesign::Pad] Pad021
  BaseFeature = -> Pocket
  Direction = (0,0,-1)
  Length = 0.8
  Length2 = 10
  Profile = -> Sketch028
  ReferenceAxis = -> Sketch028 [N_Axis]
  Type = 0
FEATURE [PartDesign::Body] Body  label="Vitre"
  Group = -> [Sketch,Pad,Fillet,Pocket,ShapeBinder003,Sketch028,Pad021]
  Origin = -> Origin056
  Tip = -> Pad021
FEATURE [PartDesign::Pocket] Pocket014
  BaseFeature = -> Pad018
  Direction = (0,2.1e-15,-1)
  Length = 0.73
  Length2 = 5
  Placement = pos=(0,0,-1.5) rot=(1,0,0;3.14159rad)
  Profile = -> Pad018 [Face67]
  Type = 0
FEATURE [PartDesign::Pocket] Pocket015
  BaseFeature = -> Pocket014
  Direction = (0,2e-15,-1)
  Length = 0.33
  Length2 = 5
  Placement = pos=(0,0,-1.5) rot=(1,0,0;3.14159rad)
  Profile = -> Pocket014 [Face113,Face111,Face117,Face116]
  Type = 0
FEATURE [Sketcher::SketchObject] Sketch029
  ExternalGeometry = -> [Pocket015]
  FullyConstrained = true
  MapMode = 5
  Placement = pos=(0,-4.7e-15,0.65) rot=(0,0,1;0rad)
  Support = -> [Pocket015]
  sketch-geometry (4):
    g0: LineSegment StartX=34.7 StartY=26.9 StartZ=0 EndX=35.1 EndY=26.9 EndZ=0
    g1: LineSegment StartX=35.1 StartY=26.9 StartZ=0 EndX=35.1 EndY=18 EndZ=0
    g2: LineSegment StartX=35.1 StartY=18 StartZ=0 EndX=34.7 EndY=18 EndZ=0
    g3: LineSegment StartX=34.7 StartY=18 StartZ=0 EndX=34.7 EndY=26.9 EndZ=0
  constraints (12):
    c: Coincident(g0,g1)
    c: Coincident(g1,g2)
    c: Coincident(g2,g3)
    c: Coincident(g3,g0)
    c: Horizontal(g0)
    c: Horizontal(g2)
    c: Vertical(g1)
    c: Vertical(g3)
    c: DistanceX(g0,g0) = 0.4
    c: DistanceY(g-4,g0) = 1
    c: DistanceY(g1,g-4) = 1
    c: DistanceX(g-3,g0) = 0.3
FEATURE [PartDesign::Pad] Pad022
  BaseFeature = -> Pocket015
  Direction = (0,-2.2e-15,1)
  Length = 5
  Length2 = 10
  Placement = pos=(0,0,-1.5) rot=(1,0,0;3.14159rad)
  Profile = -> Sketch029
  ReferenceAxis = -> Sketch029 [N_Axis]
  Type = 0
FEATURE [PartDesign::Body] Body001  label="Case_Top"
  Group = -> [DatumPlane,ReferencePocket,Sketch001,Pad001,Sketch002,Pocket001,Sketch003,Pocket002,Sketch004,Pocket003,Sketch005,Pocket004,Sketch006,Pocket005,Sketch007,Pad002,Sketch008,Pad003,Fillet001,Fillet002,Fillet003,Sketch011,Pad005,Pad006,Pad007,Fillet005,Sketch012,Pad008,Pad009,Fillet006,Fillet007,Sketch014,Pocket007,Pad010,Sketch015,Pocket008,Sketch016,ShapeBinder,Pad011,Sketch020,Pocket011,Pad016,+5 more]
  Origin = -> Origin057
  Tip = -> Pad022
FEATURE [Part::Cut] Cut  label="Case_Top_Watchy"
  Base = -> Body001
  Tool = -> Extrude
